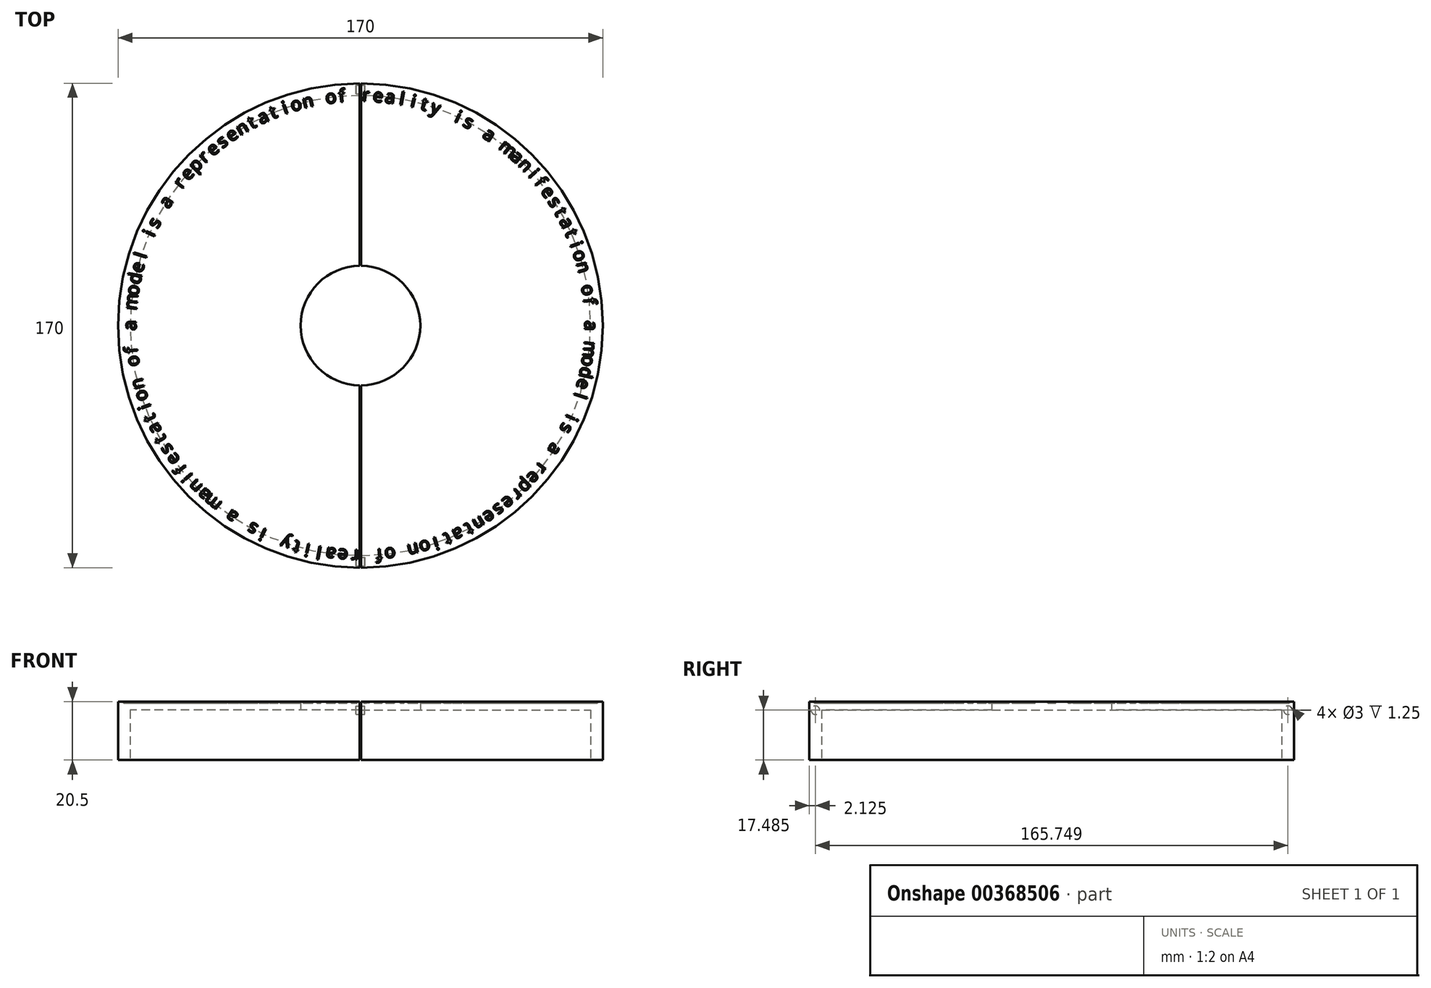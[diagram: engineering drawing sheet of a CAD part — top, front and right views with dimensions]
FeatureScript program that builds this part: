
annotation { "Feature Type Name" : "Feature", "Feature Type Description" : "" }
export const myFeature = defineFeature(function(context is Context, id is Id, definition is map)
    precondition{}
    {
        {
            var Q0;
            Q0=qCreatedBy(makeId("Front.planeOp"),FACE);
            var sketch = newSketch(context, id + "F0", { "sketchPlane" : qUnion([Q0])});
            skLineSegment(sketch, "E0", {"start": v(0, 2) * mm, "end": v(0, 7) * mm});
            skLineSegment(sketch, "E1", {"start": v(-80, 0) * mm, "end": v(-70, 0) * mm});
            skLineSegment(sketch, "E2", {"start": v(-70, 0) * mm, "end": v(-70, 2) * mm});
            skLineSegment(sketch, "E3", {"start": v(-70, 2) * mm, "end": v(0, 2) * mm});
            skLineSegment(sketch, "E4", {"start": v(0, 7) * mm, "end": v(-80, 7) * mm});
            skLineSegment(sketch, "E5", {"start": v(-80, 7) * mm, "end": v(-80, 0) * mm});
            skLineSegment(sketch, "E6.bottom", {"start": v(-21, 7) * mm, "end": v(-70, 7) * mm});
            skLineSegment(sketch, "E6.top", {"start": v(-21, 10) * mm, "end": v(-70, 10) * mm});
            skLineSegment(sketch, "E6.left", {"start": v(-21, 7) * mm, "end": v(-21, 10) * mm});
            skLineSegment(sketch, "E6.right", {"start": v(-70, 7) * mm, "end": v(-70, 10) * mm});
            skLineSegment(sketch, "E7", {"start": v(-20, 53.98) * mm, "end": v(-20, 0) * mm});
            skLineSegment(sketch, "E8", {"start": v(-20, 0) * mm, "end": v(20, 0) * mm});
            skLineSegment(sketch, "E9", {"start": v(20, 0) * mm, "end": v(20, 53.98) * mm});
            skLineSegment(sketch, "E10", {"start": v(20, 53.98) * mm, "end": v(-20, 53.98) * mm});
            skLineSegment(sketch, "E11.bottom", {"start": v(-21, 10.5) * mm, "end": v(-70.75, 10.5) * mm});
            skLineSegment(sketch, "E11.top", {"start": v(-21, 13.5) * mm, "end": v(-75, 13.5) * mm});
            skLineSegment(sketch, "E11.left", {"start": v(-21, 10.5) * mm, "end": v(-21, 13.5) * mm});
            skLineSegment(sketch, "E12.bottom", {"start": v(-21, 14) * mm, "end": v(-75.75, 14) * mm});
            skLineSegment(sketch, "E12.top", {"start": v(-21, 17) * mm, "end": v(-80, 17) * mm});
            skLineSegment(sketch, "E12.left", {"start": v(-21, 14) * mm, "end": v(-21, 17) * mm});
            skLineSegment(sketch, "E13.top", {"start": v(-80, 7) * mm, "end": v(-75.75, 7) * mm});
            skLineSegment(sketch, "E13.left", {"start": v(-80, 17) * mm, "end": v(-80, 7) * mm});
            skLineSegment(sketch, "E13.right", {"start": v(-75.75, 14) * mm, "end": v(-75.75, 7) * mm});
            skLineSegment(sketch, "E14.top", {"start": v(-75, 7) * mm, "end": v(-70.75, 7) * mm});
            skLineSegment(sketch, "E14.left", {"start": v(-75, 13.5) * mm, "end": v(-75, 7) * mm});
            skLineSegment(sketch, "E14.right", {"start": v(-70.75, 10.5) * mm, "end": v(-70.75, 7) * mm});
            skLineSegment(sketch, "E15.bottom", {"start": v(-21, 17.5) * mm, "end": v(-80.75, 17.5) * mm});
            skLineSegment(sketch, "E15.top", {"start": v(-21, 20.5) * mm, "end": v(-85, 20.5) * mm});
            skLineSegment(sketch, "E15.left", {"start": v(-21, 17.5) * mm, "end": v(-21, 20.5) * mm});
            skLineSegment(sketch, "E15.right", {"start": v(-85, 0) * mm, "end": v(-85, 20.5) * mm});
            skLineSegment(sketch, "E16.bottom", {"start": v(-85, 20.5) * mm, "end": v(-80.75, 20.5) * mm});
            skLineSegment(sketch, "E16.top", {"start": v(-85, 0) * mm, "end": v(-80.75, 0) * mm});
            skLineSegment(sketch, "E16.right", {"start": v(-80.75, 17.5) * mm, "end": v(-80.75, 0) * mm});
            skSolve(sketch);
        }
        {
            var Q0;
            Q0=makeQuery(id+"F0.imprint","IMPRINT",FACE,{"disambiguationData":[TD([[makeQuery(id+"F0.imprint","IMPRINT",EDGE,{"derivedFrom":sQuery(id+"F0.wireOp",EDGE,"E15.bottom")}),-1.0]])]});
            var Q1;
            Q1=sQuery(id+"F0.wireOp",EDGE,"E0");
            revolve(context, id + "F1", {"entities" : qUnion([Q0]), "axis" : qUnion([Q1]), "revolveType" : RevolveType.FULL});
        }
        {
            var Q0;
            Q0=makeQuery(id+"F1.opRevolve","SWEPT_FACE",FACE,{"disambiguationData":[OSD([sQuery(id+"F0.wireOp",EDGE,"E15.top"),sQuery(id+"F0.wireOp",EDGE,"E16.bottom")])]});
            var sketch = newSketch(context, id + "F2", { "sketchPlane" : qUnion([Q0])});
            skLineSegment(sketch, "E17", {"start": v(0, 0) * mm, "end": v(0, 95.11) * mm, "construction": true});
            skLineSegment(sketch, "E18.bottom", {"start": v(-1.66, 80.82) * mm, "end": v(1.34, 80.82) * mm, "construction": true});
            skLineSegment(sketch, "E18.top", {"start": v(-1.66, 76.82) * mm, "end": v(1.34, 76.82) * mm, "construction": true});
            skLineSegment(sketch, "E18.left", {"start": v(-1.66, 80.82) * mm, "end": v(-1.66, 76.82) * mm, "construction": true});
            skLineSegment(sketch, "E18.right", {"start": v(1.34, 80.82) * mm, "end": v(1.34, 76.82) * mm, "construction": true});
            skLineSegment(sketch, "E19.1.0", {"start": v(-5.82, 80.63) * mm, "end": v(-2.82, 80.78) * mm, "construction": true});
            skLineSegment(sketch, "E19.1.1", {"start": v(-2.82, 80.78) * mm, "end": v(-2.61, 76.79) * mm, "construction": true});
            skLineSegment(sketch, "E19.1.2", {"start": v(-5.6, 76.64) * mm, "end": v(-2.61, 76.79) * mm, "construction": true});
            skLineSegment(sketch, "E19.1.3", {"start": v(-5.82, 80.63) * mm, "end": v(-5.6, 76.64) * mm, "construction": true});
            skLineSegment(sketch, "E19.2.0", {"start": v(-9.96, 80.22) * mm, "end": v(-6.97, 80.53) * mm, "construction": true});
            skLineSegment(sketch, "E19.2.1", {"start": v(-6.97, 80.53) * mm, "end": v(-6.56, 76.55) * mm, "construction": true});
            skLineSegment(sketch, "E19.2.2", {"start": v(-9.55, 76.25) * mm, "end": v(-6.56, 76.55) * mm, "construction": true});
            skLineSegment(sketch, "E19.2.3", {"start": v(-9.96, 80.22) * mm, "end": v(-9.55, 76.25) * mm, "construction": true});
            skLineSegment(sketch, "E19.3.0", {"start": v(-14.08, 79.6) * mm, "end": v(-11.11, 80.07) * mm, "construction": true});
            skLineSegment(sketch, "E19.3.1", {"start": v(-11.11, 80.07) * mm, "end": v(-10.5, 76.11) * mm, "construction": true});
            skLineSegment(sketch, "E19.3.2", {"start": v(-13.46, 75.65) * mm, "end": v(-10.5, 76.11) * mm, "construction": true});
            skLineSegment(sketch, "E19.3.3", {"start": v(-14.08, 79.6) * mm, "end": v(-13.46, 75.65) * mm, "construction": true});
            skLineSegment(sketch, "E19.4.0", {"start": v(-18.15, 78.77) * mm, "end": v(-15.22, 79.39) * mm, "construction": true});
            skLineSegment(sketch, "E19.4.1", {"start": v(-15.22, 79.39) * mm, "end": v(-14.4, 75.47) * mm, "construction": true});
            skLineSegment(sketch, "E19.4.2", {"start": v(-17.34, 74.86) * mm, "end": v(-14.4, 75.47) * mm, "construction": true});
            skLineSegment(sketch, "E19.4.3", {"start": v(-18.15, 78.77) * mm, "end": v(-17.34, 74.86) * mm, "construction": true});
            skLineSegment(sketch, "E19.5.0", {"start": v(-22.19, 77.74) * mm, "end": v(-19.28, 78.5) * mm, "construction": true});
            skLineSegment(sketch, "E19.5.1", {"start": v(-19.28, 78.5) * mm, "end": v(-18.27, 74.63) * mm, "construction": true});
            skLineSegment(sketch, "E19.5.2", {"start": v(-21.17, 73.87) * mm, "end": v(-18.27, 74.63) * mm, "construction": true});
            skLineSegment(sketch, "E19.5.3", {"start": v(-22.19, 77.74) * mm, "end": v(-21.17, 73.87) * mm, "construction": true});
            skLineSegment(sketch, "E19.6.0", {"start": v(-26.16, 76.5) * mm, "end": v(-23.3, 77.4) * mm, "construction": true});
            skLineSegment(sketch, "E19.6.1", {"start": v(-23.3, 77.4) * mm, "end": v(-22.08, 73.6) * mm, "construction": true});
            skLineSegment(sketch, "E19.6.2", {"start": v(-24.94, 72.68) * mm, "end": v(-22.08, 73.6) * mm, "construction": true});
            skLineSegment(sketch, "E19.6.3", {"start": v(-26.16, 76.5) * mm, "end": v(-24.94, 72.68) * mm, "construction": true});
            skLineSegment(sketch, "E19.7.0", {"start": v(-30.06, 75.04) * mm, "end": v(-27.25, 76.1) * mm, "construction": true});
            skLineSegment(sketch, "E19.7.1", {"start": v(-27.25, 76.1) * mm, "end": v(-25.84, 72.36) * mm, "construction": true});
            skLineSegment(sketch, "E19.7.2", {"start": v(-28.65, 71.3) * mm, "end": v(-25.84, 72.36) * mm, "construction": true});
            skLineSegment(sketch, "E19.7.3", {"start": v(-30.06, 75.04) * mm, "end": v(-28.65, 71.3) * mm, "construction": true});
            skLineSegment(sketch, "E19.8.0", {"start": v(-33.88, 73.4) * mm, "end": v(-31.14, 74.6) * mm, "construction": true});
            skLineSegment(sketch, "E19.8.1", {"start": v(-31.14, 74.6) * mm, "end": v(-29.53, 70.93) * mm, "construction": true});
            skLineSegment(sketch, "E19.8.2", {"start": v(-32.28, 69.73) * mm, "end": v(-29.53, 70.93) * mm, "construction": true});
            skLineSegment(sketch, "E19.8.3", {"start": v(-33.88, 73.4) * mm, "end": v(-32.28, 69.73) * mm, "construction": true});
            skLineSegment(sketch, "E19.9.0", {"start": v(-37.62, 71.55) * mm, "end": v(-34.93, 72.9) * mm, "construction": true});
            skLineSegment(sketch, "E19.9.1", {"start": v(-34.93, 72.9) * mm, "end": v(-33.15, 69.32) * mm, "construction": true});
            skLineSegment(sketch, "E19.9.2", {"start": v(-35.83, 67.98) * mm, "end": v(-33.15, 69.32) * mm, "construction": true});
            skLineSegment(sketch, "E19.9.3", {"start": v(-37.62, 71.55) * mm, "end": v(-35.83, 67.98) * mm, "construction": true});
            skLineSegment(sketch, "E19.10.0", {"start": v(-41.25, 69.52) * mm, "end": v(-38.64, 71) * mm, "construction": true});
            skLineSegment(sketch, "E19.10.1", {"start": v(-38.64, 71) * mm, "end": v(-36.67, 67.52) * mm, "construction": true});
            skLineSegment(sketch, "E19.10.2", {"start": v(-39.28, 66.04) * mm, "end": v(-36.67, 67.52) * mm, "construction": true});
            skLineSegment(sketch, "E19.10.3", {"start": v(-41.25, 69.52) * mm, "end": v(-39.28, 66.04) * mm, "construction": true});
            skLineSegment(sketch, "E19.11.0", {"start": v(-44.78, 67.3) * mm, "end": v(-42.24, 68.92) * mm, "construction": true});
            skLineSegment(sketch, "E19.11.1", {"start": v(-42.24, 68.92) * mm, "end": v(-40.1, 65.54) * mm, "construction": true});
            skLineSegment(sketch, "E19.11.2", {"start": v(-42.63, 63.93) * mm, "end": v(-40.1, 65.54) * mm, "construction": true});
            skLineSegment(sketch, "E19.11.3", {"start": v(-44.78, 67.3) * mm, "end": v(-42.63, 63.93) * mm, "construction": true});
            skLineSegment(sketch, "E19.12.0", {"start": v(-48.18, 64.91) * mm, "end": v(-45.74, 66.65) * mm, "construction": true});
            skLineSegment(sketch, "E19.12.1", {"start": v(-45.74, 66.65) * mm, "end": v(-43.42, 63.4) * mm, "construction": true});
            skLineSegment(sketch, "E19.12.2", {"start": v(-45.86, 61.65) * mm, "end": v(-43.42, 63.4) * mm, "construction": true});
            skLineSegment(sketch, "E19.12.3", {"start": v(-48.18, 64.91) * mm, "end": v(-45.86, 61.65) * mm, "construction": true});
            skLineSegment(sketch, "E19.13.0", {"start": v(-51.46, 62.35) * mm, "end": v(-49.1, 64.2) * mm, "construction": true});
            skLineSegment(sketch, "E19.13.1", {"start": v(-49.1, 64.2) * mm, "end": v(-46.62, 61.07) * mm, "construction": true});
            skLineSegment(sketch, "E19.13.2", {"start": v(-48.98, 59.2) * mm, "end": v(-46.62, 61.07) * mm, "construction": true});
            skLineSegment(sketch, "E19.13.3", {"start": v(-51.46, 62.35) * mm, "end": v(-48.98, 59.2) * mm, "construction": true});
            skLineSegment(sketch, "E19.14.0", {"start": v(-54.6, 59.61) * mm, "end": v(-52.35, 61.6) * mm, "construction": true});
            skLineSegment(sketch, "E19.14.1", {"start": v(-52.35, 61.6) * mm, "end": v(-49.7, 58.6) * mm, "construction": true});
            skLineSegment(sketch, "E19.14.2", {"start": v(-51.96, 56.6) * mm, "end": v(-49.7, 58.6) * mm, "construction": true});
            skLineSegment(sketch, "E19.14.3", {"start": v(-54.6, 59.61) * mm, "end": v(-51.96, 56.6) * mm, "construction": true});
            skLineSegment(sketch, "E19.15.0", {"start": v(-57.6, 56.72) * mm, "end": v(-55.45, 58.82) * mm, "construction": true});
            skLineSegment(sketch, "E19.15.1", {"start": v(-55.45, 58.82) * mm, "end": v(-52.66, 55.95) * mm, "construction": true});
            skLineSegment(sketch, "E19.15.2", {"start": v(-54.8, 53.86) * mm, "end": v(-52.66, 55.95) * mm, "construction": true});
            skLineSegment(sketch, "E19.15.3", {"start": v(-57.6, 56.72) * mm, "end": v(-54.8, 53.86) * mm, "construction": true});
            skLineSegment(sketch, "E19.16.0", {"start": v(-60.44, 53.68) * mm, "end": v(-58.4, 55.89) * mm, "construction": true});
            skLineSegment(sketch, "E19.16.1", {"start": v(-58.4, 55.89) * mm, "end": v(-55.47, 53.17) * mm, "construction": true});
            skLineSegment(sketch, "E19.16.2", {"start": v(-57.5, 50.97) * mm, "end": v(-55.47, 53.17) * mm, "construction": true});
            skLineSegment(sketch, "E19.16.3", {"start": v(-60.44, 53.68) * mm, "end": v(-57.5, 50.97) * mm, "construction": true});
            skLineSegment(sketch, "E19.17.0", {"start": v(-63.12, 50.5) * mm, "end": v(-61.2, 52.8) * mm, "construction": true});
            skLineSegment(sketch, "E19.17.1", {"start": v(-61.2, 52.8) * mm, "end": v(-58.13, 50.24) * mm, "construction": true});
            skLineSegment(sketch, "E19.17.2", {"start": v(-60.05, 47.94) * mm, "end": v(-58.13, 50.24) * mm, "construction": true});
            skLineSegment(sketch, "E19.17.3", {"start": v(-63.12, 50.5) * mm, "end": v(-60.05, 47.94) * mm, "construction": true});
            skLineSegment(sketch, "E19.18.0", {"start": v(-65.64, 47.19) * mm, "end": v(-63.84, 49.58) * mm, "construction": true});
            skLineSegment(sketch, "E19.18.1", {"start": v(-63.84, 49.58) * mm, "end": v(-60.64, 47.18) * mm, "construction": true});
            skLineSegment(sketch, "E19.18.2", {"start": v(-62.44, 44.78) * mm, "end": v(-60.64, 47.18) * mm, "construction": true});
            skLineSegment(sketch, "E19.18.3", {"start": v(-65.64, 47.19) * mm, "end": v(-62.44, 44.78) * mm, "construction": true});
            skLineSegment(sketch, "E19.19.0", {"start": v(-67.98, 43.74) * mm, "end": v(-66.3, 46.23) * mm, "construction": true});
            skLineSegment(sketch, "E19.19.1", {"start": v(-66.3, 46.23) * mm, "end": v(-62.99, 44) * mm, "construction": true});
            skLineSegment(sketch, "E19.19.2", {"start": v(-64.66, 41.51) * mm, "end": v(-62.99, 44) * mm, "construction": true});
            skLineSegment(sketch, "E19.19.3", {"start": v(-67.98, 43.74) * mm, "end": v(-64.66, 41.51) * mm, "construction": true});
            skLineSegment(sketch, "E19.20.0", {"start": v(-70.14, 40.19) * mm, "end": v(-68.6, 42.76) * mm, "construction": true});
            skLineSegment(sketch, "E19.20.1", {"start": v(-68.6, 42.76) * mm, "end": v(-65.17, 40.7) * mm, "construction": true});
            skLineSegment(sketch, "E19.20.2", {"start": v(-66.71, 38.13) * mm, "end": v(-65.17, 40.7) * mm, "construction": true});
            skLineSegment(sketch, "E19.20.3", {"start": v(-70.14, 40.19) * mm, "end": v(-66.71, 38.13) * mm, "construction": true});
            skLineSegment(sketch, "E19.21.0", {"start": v(-72.12, 36.52) * mm, "end": v(-70.7, 39.17) * mm, "construction": true});
            skLineSegment(sketch, "E19.21.1", {"start": v(-70.7, 39.17) * mm, "end": v(-67.18, 37.3) * mm, "construction": true});
            skLineSegment(sketch, "E19.21.2", {"start": v(-68.59, 34.64) * mm, "end": v(-67.18, 37.3) * mm, "construction": true});
            skLineSegment(sketch, "E19.21.3", {"start": v(-72.12, 36.52) * mm, "end": v(-68.59, 34.64) * mm, "construction": true});
            skLineSegment(sketch, "E19.22.0", {"start": v(-73.9, 32.76) * mm, "end": v(-72.63, 35.48) * mm, "construction": true});
            skLineSegment(sketch, "E19.22.1", {"start": v(-72.63, 35.48) * mm, "end": v(-69, 33.78) * mm, "construction": true});
            skLineSegment(sketch, "E19.22.2", {"start": v(-70.28, 31.07) * mm, "end": v(-69, 33.78) * mm, "construction": true});
            skLineSegment(sketch, "E19.22.3", {"start": v(-73.9, 32.76) * mm, "end": v(-70.28, 31.07) * mm, "construction": true});
            skLineSegment(sketch, "E19.23.0", {"start": v(-75.5, 28.91) * mm, "end": v(-74.36, 31.7) * mm, "construction": true});
            skLineSegment(sketch, "E19.23.1", {"start": v(-74.36, 31.7) * mm, "end": v(-70.66, 30.19) * mm, "construction": true});
            skLineSegment(sketch, "E19.23.2", {"start": v(-71.79, 27.4) * mm, "end": v(-70.66, 30.19) * mm, "construction": true});
            skLineSegment(sketch, "E19.23.3", {"start": v(-75.5, 28.91) * mm, "end": v(-71.79, 27.4) * mm, "construction": true});
            skLineSegment(sketch, "E19.24.0", {"start": v(-76.88, 24.99) * mm, "end": v(-75.9, 27.82) * mm, "construction": true});
            skLineSegment(sketch, "E19.24.1", {"start": v(-75.9, 27.82) * mm, "end": v(-72.12, 26.5) * mm, "construction": true});
            skLineSegment(sketch, "E19.24.2", {"start": v(-73.1, 23.67) * mm, "end": v(-72.12, 26.5) * mm, "construction": true});
            skLineSegment(sketch, "E19.24.3", {"start": v(-76.88, 24.99) * mm, "end": v(-73.1, 23.67) * mm, "construction": true});
            skLineSegment(sketch, "E19.25.0", {"start": v(-78.07, 21) * mm, "end": v(-77.23, 23.88) * mm, "construction": true});
            skLineSegment(sketch, "E19.25.1", {"start": v(-77.23, 23.88) * mm, "end": v(-73.39, 22.76) * mm, "construction": true});
            skLineSegment(sketch, "E19.25.2", {"start": v(-74.22, 19.88) * mm, "end": v(-73.39, 22.76) * mm, "construction": true});
            skLineSegment(sketch, "E19.25.3", {"start": v(-78.07, 21) * mm, "end": v(-74.22, 19.88) * mm, "construction": true});
            skLineSegment(sketch, "E19.26.0", {"start": v(-79.04, 16.95) * mm, "end": v(-78.35, 19.87) * mm, "construction": true});
            skLineSegment(sketch, "E19.26.1", {"start": v(-78.35, 19.87) * mm, "end": v(-74.46, 18.95) * mm, "construction": true});
            skLineSegment(sketch, "E19.26.2", {"start": v(-75.15, 16.03) * mm, "end": v(-74.46, 18.95) * mm, "construction": true});
            skLineSegment(sketch, "E19.26.3", {"start": v(-79.04, 16.95) * mm, "end": v(-75.15, 16.03) * mm, "construction": true});
            skLineSegment(sketch, "E19.27.0", {"start": v(-79.81, 12.86) * mm, "end": v(-79.27, 15.81) * mm, "construction": true});
            skLineSegment(sketch, "E19.27.1", {"start": v(-79.27, 15.81) * mm, "end": v(-75.34, 15.1) * mm, "construction": true});
            skLineSegment(sketch, "E19.27.2", {"start": v(-75.88, 12.14) * mm, "end": v(-75.34, 15.1) * mm, "construction": true});
            skLineSegment(sketch, "E19.27.3", {"start": v(-79.81, 12.86) * mm, "end": v(-75.88, 12.14) * mm, "construction": true});
            skLineSegment(sketch, "E19.28.0", {"start": v(-80.37, 8.73) * mm, "end": v(-79.98, 11.7) * mm, "construction": true});
            skLineSegment(sketch, "E19.28.1", {"start": v(-79.98, 11.7) * mm, "end": v(-76.01, 11.2) * mm, "construction": true});
            skLineSegment(sketch, "E19.28.2", {"start": v(-76.4, 8.22) * mm, "end": v(-76.01, 11.2) * mm, "construction": true});
            skLineSegment(sketch, "E19.28.3", {"start": v(-80.37, 8.73) * mm, "end": v(-76.4, 8.22) * mm, "construction": true});
            skLineSegment(sketch, "E19.29.0", {"start": v(-80.7, 4.59) * mm, "end": v(-80.48, 7.58) * mm, "construction": true});
            skLineSegment(sketch, "E19.29.1", {"start": v(-80.48, 7.58) * mm, "end": v(-76.49, 7.27) * mm, "construction": true});
            skLineSegment(sketch, "E19.29.2", {"start": v(-76.72, 4.28) * mm, "end": v(-76.49, 7.27) * mm, "construction": true});
            skLineSegment(sketch, "E19.29.3", {"start": v(-80.7, 4.59) * mm, "end": v(-76.72, 4.28) * mm, "construction": true});
            skLineSegment(sketch, "E19.30.0", {"start": v(-80.84, 0.42) * mm, "end": v(-80.76, 3.42) * mm, "construction": true});
            skLineSegment(sketch, "E19.30.1", {"start": v(-80.76, 3.42) * mm, "end": v(-76.76, 3.32) * mm, "construction": true});
            skLineSegment(sketch, "E19.30.2", {"start": v(-76.84, 0.32) * mm, "end": v(-76.76, 3.32) * mm, "construction": true});
            skLineSegment(sketch, "E19.30.3", {"start": v(-80.84, 0.42) * mm, "end": v(-76.84, 0.32) * mm, "construction": true});
            skLineSegment(sketch, "E19.31.0", {"start": v(-80.75, -3.74) * mm, "end": v(-80.83, -0.74) * mm, "construction": true});
            skLineSegment(sketch, "E19.31.1", {"start": v(-80.83, -0.74) * mm, "end": v(-76.83, -0.64) * mm, "construction": true});
            skLineSegment(sketch, "E19.31.2", {"start": v(-76.75, -3.63) * mm, "end": v(-76.83, -0.64) * mm, "construction": true});
            skLineSegment(sketch, "E19.31.3", {"start": v(-80.75, -3.74) * mm, "end": v(-76.75, -3.63) * mm, "construction": true});
            skLineSegment(sketch, "E19.32.0", {"start": v(-80.45, -7.89) * mm, "end": v(-80.69, -4.9) * mm, "construction": true});
            skLineSegment(sketch, "E19.32.1", {"start": v(-80.69, -4.9) * mm, "end": v(-76.7, -4.6) * mm, "construction": true});
            skLineSegment(sketch, "E19.32.2", {"start": v(-76.47, -7.58) * mm, "end": v(-76.7, -4.6) * mm, "construction": true});
            skLineSegment(sketch, "E19.32.3", {"start": v(-80.45, -7.89) * mm, "end": v(-76.47, -7.58) * mm, "construction": true});
            skLineSegment(sketch, "E19.33.0", {"start": v(-79.94, -12.02) * mm, "end": v(-80.33, -9.05) * mm, "construction": true});
            skLineSegment(sketch, "E19.33.1", {"start": v(-80.33, -9.05) * mm, "end": v(-76.36, -8.53) * mm, "construction": true});
            skLineSegment(sketch, "E19.33.2", {"start": v(-75.97, -11.5) * mm, "end": v(-76.36, -8.53) * mm, "construction": true});
            skLineSegment(sketch, "E19.33.3", {"start": v(-79.94, -12.02) * mm, "end": v(-75.97, -11.5) * mm, "construction": true});
            skLineSegment(sketch, "E19.34.0", {"start": v(-79.22, -16.12) * mm, "end": v(-79.75, -13.17) * mm, "construction": true});
            skLineSegment(sketch, "E19.34.1", {"start": v(-79.75, -13.17) * mm, "end": v(-75.82, -12.45) * mm, "construction": true});
            skLineSegment(sketch, "E19.34.2", {"start": v(-75.28, -15.4) * mm, "end": v(-75.82, -12.45) * mm, "construction": true});
            skLineSegment(sketch, "E19.34.3", {"start": v(-79.22, -16.12) * mm, "end": v(-75.28, -15.4) * mm, "construction": true});
            skLineSegment(sketch, "E19.35.0", {"start": v(-78.28, -20.18) * mm, "end": v(-78.97, -17.26) * mm, "construction": true});
            skLineSegment(sketch, "E19.35.1", {"start": v(-78.97, -17.26) * mm, "end": v(-75.08, -16.34) * mm, "construction": true});
            skLineSegment(sketch, "E19.35.2", {"start": v(-74.39, -19.26) * mm, "end": v(-75.08, -16.34) * mm, "construction": true});
            skLineSegment(sketch, "E19.35.3", {"start": v(-78.28, -20.18) * mm, "end": v(-74.39, -19.26) * mm, "construction": true});
            skLineSegment(sketch, "E19.36.0", {"start": v(-77.14, -24.18) * mm, "end": v(-77.98, -21.3) * mm, "construction": true});
            skLineSegment(sketch, "E19.36.1", {"start": v(-77.98, -21.3) * mm, "end": v(-74.14, -20.18) * mm, "construction": true});
            skLineSegment(sketch, "E19.36.2", {"start": v(-73.3, -23.06) * mm, "end": v(-74.14, -20.18) * mm, "construction": true});
            skLineSegment(sketch, "E19.36.3", {"start": v(-77.14, -24.18) * mm, "end": v(-73.3, -23.06) * mm, "construction": true});
            skLineSegment(sketch, "E19.37.0", {"start": v(-75.8, -28.12) * mm, "end": v(-76.78, -25.29) * mm, "construction": true});
            skLineSegment(sketch, "E19.37.1", {"start": v(-76.78, -25.29) * mm, "end": v(-73, -23.97) * mm, "construction": true});
            skLineSegment(sketch, "E19.37.2", {"start": v(-72.01, -26.8) * mm, "end": v(-73, -23.97) * mm, "construction": true});
            skLineSegment(sketch, "E19.37.3", {"start": v(-75.8, -28.12) * mm, "end": v(-72.01, -26.8) * mm, "construction": true});
            skLineSegment(sketch, "E19.38.0", {"start": v(-74.24, -31.98) * mm, "end": v(-75.37, -29.2) * mm, "construction": true});
            skLineSegment(sketch, "E19.38.1", {"start": v(-75.37, -29.2) * mm, "end": v(-71.67, -27.7) * mm, "construction": true});
            skLineSegment(sketch, "E19.38.2", {"start": v(-70.54, -30.48) * mm, "end": v(-71.67, -27.7) * mm, "construction": true});
            skLineSegment(sketch, "E19.38.3", {"start": v(-74.24, -31.98) * mm, "end": v(-70.54, -30.48) * mm, "construction": true});
            skLineSegment(sketch, "E19.39.0", {"start": v(-72.5, -35.76) * mm, "end": v(-73.77, -33.05) * mm, "construction": true});
            skLineSegment(sketch, "E19.39.1", {"start": v(-73.77, -33.05) * mm, "end": v(-70.15, -31.35) * mm, "construction": true});
            skLineSegment(sketch, "E19.39.2", {"start": v(-68.88, -34.07) * mm, "end": v(-70.15, -31.35) * mm, "construction": true});
            skLineSegment(sketch, "E19.39.3", {"start": v(-72.5, -35.76) * mm, "end": v(-68.88, -34.07) * mm, "construction": true});
            skLineSegment(sketch, "E19.40.0", {"start": v(-70.56, -39.45) * mm, "end": v(-71.97, -36.8) * mm, "construction": true});
            skLineSegment(sketch, "E19.40.1", {"start": v(-71.97, -36.8) * mm, "end": v(-68.44, -34.92) * mm, "construction": true});
            skLineSegment(sketch, "E19.40.2", {"start": v(-67.03, -37.57) * mm, "end": v(-68.44, -34.92) * mm, "construction": true});
            skLineSegment(sketch, "E19.40.3", {"start": v(-70.56, -39.45) * mm, "end": v(-67.03, -37.57) * mm, "construction": true});
            skLineSegment(sketch, "E19.41.0", {"start": v(-68.44, -43.03) * mm, "end": v(-69.98, -40.46) * mm, "construction": true});
            skLineSegment(sketch, "E19.41.1", {"start": v(-69.98, -40.46) * mm, "end": v(-66.55, -38.4) * mm, "construction": true});
            skLineSegment(sketch, "E19.41.2", {"start": v(-65, -40.97) * mm, "end": v(-66.55, -38.4) * mm, "construction": true});
            skLineSegment(sketch, "E19.41.3", {"start": v(-68.44, -43.03) * mm, "end": v(-65, -40.97) * mm, "construction": true});
            skLineSegment(sketch, "E19.42.0", {"start": v(-66.13, -46.5) * mm, "end": v(-67.8, -44) * mm, "construction": true});
            skLineSegment(sketch, "E19.42.1", {"start": v(-67.8, -44) * mm, "end": v(-64.49, -41.77) * mm, "construction": true});
            skLineSegment(sketch, "E19.42.2", {"start": v(-62.81, -44.26) * mm, "end": v(-64.49, -41.77) * mm, "construction": true});
            skLineSegment(sketch, "E19.42.3", {"start": v(-66.13, -46.5) * mm, "end": v(-62.81, -44.26) * mm, "construction": true});
            skLineSegment(sketch, "E19.43.0", {"start": v(-63.65, -49.84) * mm, "end": v(-65.45, -47.44) * mm, "construction": true});
            skLineSegment(sketch, "E19.43.1", {"start": v(-65.45, -47.44) * mm, "end": v(-62.25, -45.04) * mm, "construction": true});
            skLineSegment(sketch, "E19.43.2", {"start": v(-60.45, -47.44) * mm, "end": v(-62.25, -45.04) * mm, "construction": true});
            skLineSegment(sketch, "E19.43.3", {"start": v(-63.65, -49.84) * mm, "end": v(-60.45, -47.44) * mm, "construction": true});
            skLineSegment(sketch, "E19.44.0", {"start": v(-61, -53.05) * mm, "end": v(-62.92, -50.74) * mm, "construction": true});
            skLineSegment(sketch, "E19.44.1", {"start": v(-62.92, -50.74) * mm, "end": v(-59.85, -48.18) * mm, "construction": true});
            skLineSegment(sketch, "E19.44.2", {"start": v(-57.93, -50.48) * mm, "end": v(-59.85, -48.18) * mm, "construction": true});
            skLineSegment(sketch, "E19.44.3", {"start": v(-61, -53.05) * mm, "end": v(-57.93, -50.48) * mm, "construction": true});
            skLineSegment(sketch, "E19.45.0", {"start": v(-58.19, -56.12) * mm, "end": v(-60.23, -53.92) * mm, "construction": true});
            skLineSegment(sketch, "E19.45.1", {"start": v(-60.23, -53.92) * mm, "end": v(-57.3, -51.2) * mm, "construction": true});
            skLineSegment(sketch, "E19.45.2", {"start": v(-55.25, -53.4) * mm, "end": v(-57.3, -51.2) * mm, "construction": true});
            skLineSegment(sketch, "E19.45.3", {"start": v(-58.19, -56.12) * mm, "end": v(-55.25, -53.4) * mm, "construction": true});
            skLineSegment(sketch, "E19.46.0", {"start": v(-55.22, -59.04) * mm, "end": v(-57.37, -56.94) * mm, "construction": true});
            skLineSegment(sketch, "E19.46.1", {"start": v(-57.37, -56.94) * mm, "end": v(-54.58, -54.08) * mm, "construction": true});
            skLineSegment(sketch, "E19.46.2", {"start": v(-52.43, -56.17) * mm, "end": v(-54.58, -54.08) * mm, "construction": true});
            skLineSegment(sketch, "E19.46.3", {"start": v(-55.22, -59.04) * mm, "end": v(-52.43, -56.17) * mm, "construction": true});
            skLineSegment(sketch, "E19.47.0", {"start": v(-52.11, -61.8) * mm, "end": v(-54.36, -59.82) * mm, "construction": true});
            skLineSegment(sketch, "E19.47.1", {"start": v(-54.36, -59.82) * mm, "end": v(-51.72, -56.82) * mm, "construction": true});
            skLineSegment(sketch, "E19.47.2", {"start": v(-49.47, -58.8) * mm, "end": v(-51.72, -56.82) * mm, "construction": true});
            skLineSegment(sketch, "E19.47.3", {"start": v(-52.11, -61.8) * mm, "end": v(-49.47, -58.8) * mm, "construction": true});
            skLineSegment(sketch, "E19.48.0", {"start": v(-48.86, -64.4) * mm, "end": v(-51.21, -62.54) * mm, "construction": true});
            skLineSegment(sketch, "E19.48.1", {"start": v(-51.21, -62.54) * mm, "end": v(-48.73, -59.4) * mm, "construction": true});
            skLineSegment(sketch, "E19.48.2", {"start": v(-46.38, -61.27) * mm, "end": v(-48.73, -59.4) * mm, "construction": true});
            skLineSegment(sketch, "E19.48.3", {"start": v(-48.86, -64.4) * mm, "end": v(-46.38, -61.27) * mm, "construction": true});
            skLineSegment(sketch, "E19.49.0", {"start": v(-45.48, -66.83) * mm, "end": v(-47.92, -65.1) * mm, "construction": true});
            skLineSegment(sketch, "E19.49.1", {"start": v(-47.92, -65.1) * mm, "end": v(-45.6, -61.83) * mm, "construction": true});
            skLineSegment(sketch, "E19.49.2", {"start": v(-43.16, -63.57) * mm, "end": v(-45.6, -61.83) * mm, "construction": true});
            skLineSegment(sketch, "E19.49.3", {"start": v(-45.48, -66.83) * mm, "end": v(-43.16, -63.57) * mm, "construction": true});
            skLineSegment(sketch, "E19.50.0", {"start": v(-41.98, -69.09) * mm, "end": v(-44.51, -67.48) * mm, "construction": true});
            skLineSegment(sketch, "E19.50.1", {"start": v(-44.51, -67.48) * mm, "end": v(-42.36, -64.1) * mm, "construction": true});
            skLineSegment(sketch, "E19.50.2", {"start": v(-39.83, -65.71) * mm, "end": v(-42.36, -64.1) * mm, "construction": true});
            skLineSegment(sketch, "E19.50.3", {"start": v(-41.98, -69.09) * mm, "end": v(-39.83, -65.71) * mm, "construction": true});
            skLineSegment(sketch, "E19.51.0", {"start": v(-38.37, -71.16) * mm, "end": v(-40.98, -69.68) * mm, "construction": true});
            skLineSegment(sketch, "E19.51.1", {"start": v(-40.98, -69.68) * mm, "end": v(-39, -66.2) * mm, "construction": true});
            skLineSegment(sketch, "E19.51.2", {"start": v(-36.4, -67.67) * mm, "end": v(-39, -66.2) * mm, "construction": true});
            skLineSegment(sketch, "E19.51.3", {"start": v(-38.37, -71.16) * mm, "end": v(-36.4, -67.67) * mm, "construction": true});
            skLineSegment(sketch, "E19.52.0", {"start": v(-34.65, -73.04) * mm, "end": v(-37.34, -71.7) * mm, "construction": true});
            skLineSegment(sketch, "E19.52.1", {"start": v(-37.34, -71.7) * mm, "end": v(-35.55, -68.12) * mm, "construction": true});
            skLineSegment(sketch, "E19.52.2", {"start": v(-32.86, -69.46) * mm, "end": v(-35.55, -68.12) * mm, "construction": true});
            skLineSegment(sketch, "E19.52.3", {"start": v(-34.65, -73.04) * mm, "end": v(-32.86, -69.46) * mm, "construction": true});
            skLineSegment(sketch, "E19.53.0", {"start": v(-30.85, -74.72) * mm, "end": v(-33.6, -73.52) * mm, "construction": true});
            skLineSegment(sketch, "E19.53.1", {"start": v(-33.6, -73.52) * mm, "end": v(-32, -69.86) * mm, "construction": true});
            skLineSegment(sketch, "E19.53.2", {"start": v(-29.25, -71.06) * mm, "end": v(-32, -69.86) * mm, "construction": true});
            skLineSegment(sketch, "E19.53.3", {"start": v(-30.85, -74.72) * mm, "end": v(-29.25, -71.06) * mm, "construction": true});
            skLineSegment(sketch, "E19.54.0", {"start": v(-26.96, -76.21) * mm, "end": v(-29.77, -75.15) * mm, "construction": true});
            skLineSegment(sketch, "E19.54.1", {"start": v(-29.77, -75.15) * mm, "end": v(-28.36, -71.41) * mm, "construction": true});
            skLineSegment(sketch, "E19.54.2", {"start": v(-25.55, -72.47) * mm, "end": v(-28.36, -71.41) * mm, "construction": true});
            skLineSegment(sketch, "E19.54.3", {"start": v(-26.96, -76.21) * mm, "end": v(-25.55, -72.47) * mm, "construction": true});
            skLineSegment(sketch, "E19.55.0", {"start": v(-23, -77.5) * mm, "end": v(-25.86, -76.59) * mm, "construction": true});
            skLineSegment(sketch, "E19.55.1", {"start": v(-25.86, -76.59) * mm, "end": v(-24.64, -72.78) * mm, "construction": true});
            skLineSegment(sketch, "E19.55.2", {"start": v(-21.78, -73.69) * mm, "end": v(-24.64, -72.78) * mm, "construction": true});
            skLineSegment(sketch, "E19.55.3", {"start": v(-23, -77.5) * mm, "end": v(-21.78, -73.69) * mm, "construction": true});
            skLineSegment(sketch, "E19.56.0", {"start": v(-18.98, -78.58) * mm, "end": v(-21.88, -77.82) * mm, "construction": true});
            skLineSegment(sketch, "E19.56.1", {"start": v(-21.88, -77.82) * mm, "end": v(-20.86, -73.95) * mm, "construction": true});
            skLineSegment(sketch, "E19.56.2", {"start": v(-17.96, -74.71) * mm, "end": v(-20.86, -73.95) * mm, "construction": true});
            skLineSegment(sketch, "E19.56.3", {"start": v(-18.98, -78.58) * mm, "end": v(-17.96, -74.71) * mm, "construction": true});
            skLineSegment(sketch, "E19.57.0", {"start": v(-14.91, -79.45) * mm, "end": v(-17.85, -78.84) * mm, "construction": true});
            skLineSegment(sketch, "E19.57.1", {"start": v(-17.85, -78.84) * mm, "end": v(-17.03, -74.92) * mm, "construction": true});
            skLineSegment(sketch, "E19.57.2", {"start": v(-14.1, -75.54) * mm, "end": v(-17.03, -74.92) * mm, "construction": true});
            skLineSegment(sketch, "E19.57.3", {"start": v(-14.91, -79.45) * mm, "end": v(-14.1, -75.54) * mm, "construction": true});
            skLineSegment(sketch, "E19.58.0", {"start": v(-10.8, -80.11) * mm, "end": v(-13.76, -79.65) * mm, "construction": true});
            skLineSegment(sketch, "E19.58.1", {"start": v(-13.76, -79.65) * mm, "end": v(-13.15, -75.7) * mm, "construction": true});
            skLineSegment(sketch, "E19.58.2", {"start": v(-10.18, -76.16) * mm, "end": v(-13.15, -75.7) * mm, "construction": true});
            skLineSegment(sketch, "E19.58.3", {"start": v(-10.8, -80.11) * mm, "end": v(-10.18, -76.16) * mm, "construction": true});
            skLineSegment(sketch, "E19.59.0", {"start": v(-6.66, -80.56) * mm, "end": v(-9.65, -80.26) * mm, "construction": true});
            skLineSegment(sketch, "E19.59.1", {"start": v(-9.65, -80.26) * mm, "end": v(-9.23, -76.28) * mm, "construction": true});
            skLineSegment(sketch, "E19.59.2", {"start": v(-6.25, -76.59) * mm, "end": v(-9.23, -76.28) * mm, "construction": true});
            skLineSegment(sketch, "E19.59.3", {"start": v(-6.66, -80.56) * mm, "end": v(-6.25, -76.59) * mm, "construction": true});
            skLineSegment(sketch, "E19.60.0", {"start": v(-2.5, -80.8) * mm, "end": v(-5.5, -80.65) * mm, "construction": true});
            skLineSegment(sketch, "E19.60.1", {"start": v(-5.5, -80.65) * mm, "end": v(-5.3, -76.65) * mm, "construction": true});
            skLineSegment(sketch, "E19.60.2", {"start": v(-2.3, -76.8) * mm, "end": v(-5.3, -76.65) * mm, "construction": true});
            skLineSegment(sketch, "E19.60.3", {"start": v(-2.5, -80.8) * mm, "end": v(-2.3, -76.8) * mm, "construction": true});
            skLineSegment(sketch, "E19.61.0", {"start": v(1.66, -80.82) * mm, "end": v(-1.34, -80.82) * mm, "construction": true});
            skLineSegment(sketch, "E19.61.1", {"start": v(-1.34, -80.82) * mm, "end": v(-1.34, -76.82) * mm, "construction": true});
            skLineSegment(sketch, "E19.61.2", {"start": v(1.66, -76.82) * mm, "end": v(-1.34, -76.82) * mm, "construction": true});
            skLineSegment(sketch, "E19.61.3", {"start": v(1.66, -80.82) * mm, "end": v(1.66, -76.82) * mm, "construction": true});
            skLineSegment(sketch, "E19.62.0", {"start": v(5.82, -80.63) * mm, "end": v(2.82, -80.78) * mm, "construction": true});
            skLineSegment(sketch, "E19.62.1", {"start": v(2.82, -80.78) * mm, "end": v(2.61, -76.79) * mm, "construction": true});
            skLineSegment(sketch, "E19.62.2", {"start": v(5.6, -76.64) * mm, "end": v(2.61, -76.79) * mm, "construction": true});
            skLineSegment(sketch, "E19.62.3", {"start": v(5.82, -80.63) * mm, "end": v(5.6, -76.64) * mm, "construction": true});
            skLineSegment(sketch, "E19.63.0", {"start": v(9.96, -80.22) * mm, "end": v(6.97, -80.53) * mm, "construction": true});
            skLineSegment(sketch, "E19.63.1", {"start": v(6.97, -80.53) * mm, "end": v(6.56, -76.55) * mm, "construction": true});
            skLineSegment(sketch, "E19.63.2", {"start": v(9.55, -76.25) * mm, "end": v(6.56, -76.55) * mm, "construction": true});
            skLineSegment(sketch, "E19.63.3", {"start": v(9.96, -80.22) * mm, "end": v(9.55, -76.25) * mm, "construction": true});
            skLineSegment(sketch, "E19.64.0", {"start": v(14.08, -79.6) * mm, "end": v(11.11, -80.07) * mm, "construction": true});
            skLineSegment(sketch, "E19.64.1", {"start": v(11.11, -80.07) * mm, "end": v(10.5, -76.11) * mm, "construction": true});
            skLineSegment(sketch, "E19.64.2", {"start": v(13.46, -75.65) * mm, "end": v(10.5, -76.11) * mm, "construction": true});
            skLineSegment(sketch, "E19.64.3", {"start": v(14.08, -79.6) * mm, "end": v(13.46, -75.65) * mm, "construction": true});
            skLineSegment(sketch, "E19.65.0", {"start": v(18.15, -78.77) * mm, "end": v(15.22, -79.39) * mm, "construction": true});
            skLineSegment(sketch, "E19.65.1", {"start": v(15.22, -79.39) * mm, "end": v(14.4, -75.47) * mm, "construction": true});
            skLineSegment(sketch, "E19.65.2", {"start": v(17.34, -74.86) * mm, "end": v(14.4, -75.47) * mm, "construction": true});
            skLineSegment(sketch, "E19.65.3", {"start": v(18.15, -78.77) * mm, "end": v(17.34, -74.86) * mm, "construction": true});
            skLineSegment(sketch, "E19.66.0", {"start": v(22.19, -77.74) * mm, "end": v(19.28, -78.5) * mm, "construction": true});
            skLineSegment(sketch, "E19.66.1", {"start": v(19.28, -78.5) * mm, "end": v(18.27, -74.63) * mm, "construction": true});
            skLineSegment(sketch, "E19.66.2", {"start": v(21.17, -73.87) * mm, "end": v(18.27, -74.63) * mm, "construction": true});
            skLineSegment(sketch, "E19.66.3", {"start": v(22.19, -77.74) * mm, "end": v(21.17, -73.87) * mm, "construction": true});
            skLineSegment(sketch, "E19.67.0", {"start": v(26.16, -76.5) * mm, "end": v(23.3, -77.4) * mm, "construction": true});
            skLineSegment(sketch, "E19.67.1", {"start": v(23.3, -77.4) * mm, "end": v(22.08, -73.6) * mm, "construction": true});
            skLineSegment(sketch, "E19.67.2", {"start": v(24.94, -72.68) * mm, "end": v(22.08, -73.6) * mm, "construction": true});
            skLineSegment(sketch, "E19.67.3", {"start": v(26.16, -76.5) * mm, "end": v(24.94, -72.68) * mm, "construction": true});
            skLineSegment(sketch, "E19.68.0", {"start": v(30.06, -75.04) * mm, "end": v(27.25, -76.1) * mm, "construction": true});
            skLineSegment(sketch, "E19.68.1", {"start": v(27.25, -76.1) * mm, "end": v(25.84, -72.36) * mm, "construction": true});
            skLineSegment(sketch, "E19.68.2", {"start": v(28.65, -71.3) * mm, "end": v(25.84, -72.36) * mm, "construction": true});
            skLineSegment(sketch, "E19.68.3", {"start": v(30.06, -75.04) * mm, "end": v(28.65, -71.3) * mm, "construction": true});
            skLineSegment(sketch, "E19.69.0", {"start": v(33.88, -73.4) * mm, "end": v(31.14, -74.6) * mm, "construction": true});
            skLineSegment(sketch, "E19.69.1", {"start": v(31.14, -74.6) * mm, "end": v(29.53, -70.93) * mm, "construction": true});
            skLineSegment(sketch, "E19.69.2", {"start": v(32.28, -69.73) * mm, "end": v(29.53, -70.93) * mm, "construction": true});
            skLineSegment(sketch, "E19.69.3", {"start": v(33.88, -73.4) * mm, "end": v(32.28, -69.73) * mm, "construction": true});
            skLineSegment(sketch, "E19.70.0", {"start": v(37.62, -71.55) * mm, "end": v(34.93, -72.9) * mm, "construction": true});
            skLineSegment(sketch, "E19.70.1", {"start": v(34.93, -72.9) * mm, "end": v(33.15, -69.32) * mm, "construction": true});
            skLineSegment(sketch, "E19.70.2", {"start": v(35.83, -67.98) * mm, "end": v(33.15, -69.32) * mm, "construction": true});
            skLineSegment(sketch, "E19.70.3", {"start": v(37.62, -71.55) * mm, "end": v(35.83, -67.98) * mm, "construction": true});
            skLineSegment(sketch, "E19.71.0", {"start": v(41.25, -69.52) * mm, "end": v(38.64, -71) * mm, "construction": true});
            skLineSegment(sketch, "E19.71.1", {"start": v(38.64, -71) * mm, "end": v(36.67, -67.52) * mm, "construction": true});
            skLineSegment(sketch, "E19.71.2", {"start": v(39.28, -66.04) * mm, "end": v(36.67, -67.52) * mm, "construction": true});
            skLineSegment(sketch, "E19.71.3", {"start": v(41.25, -69.52) * mm, "end": v(39.28, -66.04) * mm, "construction": true});
            skLineSegment(sketch, "E19.72.0", {"start": v(44.78, -67.3) * mm, "end": v(42.24, -68.92) * mm, "construction": true});
            skLineSegment(sketch, "E19.72.1", {"start": v(42.24, -68.92) * mm, "end": v(40.1, -65.54) * mm, "construction": true});
            skLineSegment(sketch, "E19.72.2", {"start": v(42.63, -63.93) * mm, "end": v(40.1, -65.54) * mm, "construction": true});
            skLineSegment(sketch, "E19.72.3", {"start": v(44.78, -67.3) * mm, "end": v(42.63, -63.93) * mm, "construction": true});
            skLineSegment(sketch, "E19.73.0", {"start": v(48.18, -64.91) * mm, "end": v(45.74, -66.65) * mm, "construction": true});
            skLineSegment(sketch, "E19.73.1", {"start": v(45.74, -66.65) * mm, "end": v(43.42, -63.4) * mm, "construction": true});
            skLineSegment(sketch, "E19.73.2", {"start": v(45.86, -61.65) * mm, "end": v(43.42, -63.4) * mm, "construction": true});
            skLineSegment(sketch, "E19.73.3", {"start": v(48.18, -64.91) * mm, "end": v(45.86, -61.65) * mm, "construction": true});
            skLineSegment(sketch, "E19.74.0", {"start": v(51.46, -62.35) * mm, "end": v(49.1, -64.2) * mm, "construction": true});
            skLineSegment(sketch, "E19.74.1", {"start": v(49.1, -64.2) * mm, "end": v(46.62, -61.07) * mm, "construction": true});
            skLineSegment(sketch, "E19.74.2", {"start": v(48.98, -59.2) * mm, "end": v(46.62, -61.07) * mm, "construction": true});
            skLineSegment(sketch, "E19.74.3", {"start": v(51.46, -62.35) * mm, "end": v(48.98, -59.2) * mm, "construction": true});
            skLineSegment(sketch, "E19.75.0", {"start": v(54.6, -59.61) * mm, "end": v(52.35, -61.6) * mm, "construction": true});
            skLineSegment(sketch, "E19.75.1", {"start": v(52.35, -61.6) * mm, "end": v(49.7, -58.6) * mm, "construction": true});
            skLineSegment(sketch, "E19.75.2", {"start": v(51.96, -56.6) * mm, "end": v(49.7, -58.6) * mm, "construction": true});
            skLineSegment(sketch, "E19.75.3", {"start": v(54.6, -59.61) * mm, "end": v(51.96, -56.6) * mm, "construction": true});
            skLineSegment(sketch, "E19.76.0", {"start": v(57.6, -56.72) * mm, "end": v(55.45, -58.82) * mm, "construction": true});
            skLineSegment(sketch, "E19.76.1", {"start": v(55.45, -58.82) * mm, "end": v(52.66, -55.95) * mm, "construction": true});
            skLineSegment(sketch, "E19.76.2", {"start": v(54.8, -53.86) * mm, "end": v(52.66, -55.95) * mm, "construction": true});
            skLineSegment(sketch, "E19.76.3", {"start": v(57.6, -56.72) * mm, "end": v(54.8, -53.86) * mm, "construction": true});
            skLineSegment(sketch, "E19.77.0", {"start": v(60.44, -53.68) * mm, "end": v(58.4, -55.89) * mm, "construction": true});
            skLineSegment(sketch, "E19.77.1", {"start": v(58.4, -55.89) * mm, "end": v(55.47, -53.17) * mm, "construction": true});
            skLineSegment(sketch, "E19.77.2", {"start": v(57.5, -50.97) * mm, "end": v(55.47, -53.17) * mm, "construction": true});
            skLineSegment(sketch, "E19.77.3", {"start": v(60.44, -53.68) * mm, "end": v(57.5, -50.97) * mm, "construction": true});
            skLineSegment(sketch, "E19.78.0", {"start": v(63.12, -50.5) * mm, "end": v(61.2, -52.8) * mm, "construction": true});
            skLineSegment(sketch, "E19.78.1", {"start": v(61.2, -52.8) * mm, "end": v(58.13, -50.24) * mm, "construction": true});
            skLineSegment(sketch, "E19.78.2", {"start": v(60.05, -47.94) * mm, "end": v(58.13, -50.24) * mm, "construction": true});
            skLineSegment(sketch, "E19.78.3", {"start": v(63.12, -50.5) * mm, "end": v(60.05, -47.94) * mm, "construction": true});
            skLineSegment(sketch, "E19.79.0", {"start": v(65.64, -47.19) * mm, "end": v(63.84, -49.58) * mm, "construction": true});
            skLineSegment(sketch, "E19.79.1", {"start": v(63.84, -49.58) * mm, "end": v(60.64, -47.18) * mm, "construction": true});
            skLineSegment(sketch, "E19.79.2", {"start": v(62.44, -44.78) * mm, "end": v(60.64, -47.18) * mm, "construction": true});
            skLineSegment(sketch, "E19.79.3", {"start": v(65.64, -47.19) * mm, "end": v(62.44, -44.78) * mm, "construction": true});
            skLineSegment(sketch, "E19.80.0", {"start": v(67.98, -43.74) * mm, "end": v(66.3, -46.23) * mm, "construction": true});
            skLineSegment(sketch, "E19.80.1", {"start": v(66.3, -46.23) * mm, "end": v(62.99, -44) * mm, "construction": true});
            skLineSegment(sketch, "E19.80.2", {"start": v(64.66, -41.51) * mm, "end": v(62.99, -44) * mm, "construction": true});
            skLineSegment(sketch, "E19.80.3", {"start": v(67.98, -43.74) * mm, "end": v(64.66, -41.51) * mm, "construction": true});
            skLineSegment(sketch, "E19.81.0", {"start": v(70.14, -40.19) * mm, "end": v(68.6, -42.76) * mm, "construction": true});
            skLineSegment(sketch, "E19.81.1", {"start": v(68.6, -42.76) * mm, "end": v(65.17, -40.7) * mm, "construction": true});
            skLineSegment(sketch, "E19.81.2", {"start": v(66.71, -38.13) * mm, "end": v(65.17, -40.7) * mm, "construction": true});
            skLineSegment(sketch, "E19.81.3", {"start": v(70.14, -40.19) * mm, "end": v(66.71, -38.13) * mm, "construction": true});
            skLineSegment(sketch, "E19.82.0", {"start": v(72.12, -36.52) * mm, "end": v(70.7, -39.17) * mm, "construction": true});
            skLineSegment(sketch, "E19.82.1", {"start": v(70.7, -39.17) * mm, "end": v(67.18, -37.3) * mm, "construction": true});
            skLineSegment(sketch, "E19.82.2", {"start": v(68.59, -34.64) * mm, "end": v(67.18, -37.3) * mm, "construction": true});
            skLineSegment(sketch, "E19.82.3", {"start": v(72.12, -36.52) * mm, "end": v(68.59, -34.64) * mm, "construction": true});
            skLineSegment(sketch, "E19.83.0", {"start": v(73.9, -32.76) * mm, "end": v(72.63, -35.48) * mm, "construction": true});
            skLineSegment(sketch, "E19.83.1", {"start": v(72.63, -35.48) * mm, "end": v(69, -33.78) * mm, "construction": true});
            skLineSegment(sketch, "E19.83.2", {"start": v(70.28, -31.07) * mm, "end": v(69, -33.78) * mm, "construction": true});
            skLineSegment(sketch, "E19.83.3", {"start": v(73.9, -32.76) * mm, "end": v(70.28, -31.07) * mm, "construction": true});
            skLineSegment(sketch, "E19.84.0", {"start": v(75.5, -28.91) * mm, "end": v(74.36, -31.7) * mm, "construction": true});
            skLineSegment(sketch, "E19.84.1", {"start": v(74.36, -31.7) * mm, "end": v(70.66, -30.19) * mm, "construction": true});
            skLineSegment(sketch, "E19.84.2", {"start": v(71.79, -27.4) * mm, "end": v(70.66, -30.19) * mm, "construction": true});
            skLineSegment(sketch, "E19.84.3", {"start": v(75.5, -28.91) * mm, "end": v(71.79, -27.4) * mm, "construction": true});
            skLineSegment(sketch, "E19.85.0", {"start": v(76.88, -24.99) * mm, "end": v(75.9, -27.82) * mm, "construction": true});
            skLineSegment(sketch, "E19.85.1", {"start": v(75.9, -27.82) * mm, "end": v(72.12, -26.5) * mm, "construction": true});
            skLineSegment(sketch, "E19.85.2", {"start": v(73.1, -23.67) * mm, "end": v(72.12, -26.5) * mm, "construction": true});
            skLineSegment(sketch, "E19.85.3", {"start": v(76.88, -24.99) * mm, "end": v(73.1, -23.67) * mm, "construction": true});
            skLineSegment(sketch, "E19.86.0", {"start": v(78.07, -21) * mm, "end": v(77.23, -23.88) * mm, "construction": true});
            skLineSegment(sketch, "E19.86.1", {"start": v(77.23, -23.88) * mm, "end": v(73.39, -22.76) * mm, "construction": true});
            skLineSegment(sketch, "E19.86.2", {"start": v(74.22, -19.88) * mm, "end": v(73.39, -22.76) * mm, "construction": true});
            skLineSegment(sketch, "E19.86.3", {"start": v(78.07, -21) * mm, "end": v(74.22, -19.88) * mm, "construction": true});
            skLineSegment(sketch, "E19.87.0", {"start": v(79.04, -16.95) * mm, "end": v(78.35, -19.87) * mm, "construction": true});
            skLineSegment(sketch, "E19.87.1", {"start": v(78.35, -19.87) * mm, "end": v(74.46, -18.95) * mm, "construction": true});
            skLineSegment(sketch, "E19.87.2", {"start": v(75.15, -16.03) * mm, "end": v(74.46, -18.95) * mm, "construction": true});
            skLineSegment(sketch, "E19.87.3", {"start": v(79.04, -16.95) * mm, "end": v(75.15, -16.03) * mm, "construction": true});
            skLineSegment(sketch, "E19.88.0", {"start": v(79.81, -12.86) * mm, "end": v(79.27, -15.81) * mm, "construction": true});
            skLineSegment(sketch, "E19.88.1", {"start": v(79.27, -15.81) * mm, "end": v(75.34, -15.1) * mm, "construction": true});
            skLineSegment(sketch, "E19.88.2", {"start": v(75.88, -12.14) * mm, "end": v(75.34, -15.1) * mm, "construction": true});
            skLineSegment(sketch, "E19.88.3", {"start": v(79.81, -12.86) * mm, "end": v(75.88, -12.14) * mm, "construction": true});
            skLineSegment(sketch, "E19.89.0", {"start": v(80.37, -8.73) * mm, "end": v(79.98, -11.7) * mm, "construction": true});
            skLineSegment(sketch, "E19.89.1", {"start": v(79.98, -11.7) * mm, "end": v(76.01, -11.2) * mm, "construction": true});
            skLineSegment(sketch, "E19.89.2", {"start": v(76.4, -8.22) * mm, "end": v(76.01, -11.2) * mm, "construction": true});
            skLineSegment(sketch, "E19.89.3", {"start": v(80.37, -8.73) * mm, "end": v(76.4, -8.22) * mm, "construction": true});
            skLineSegment(sketch, "E19.90.0", {"start": v(80.7, -4.59) * mm, "end": v(80.48, -7.58) * mm, "construction": true});
            skLineSegment(sketch, "E19.90.1", {"start": v(80.48, -7.58) * mm, "end": v(76.49, -7.27) * mm, "construction": true});
            skLineSegment(sketch, "E19.90.2", {"start": v(76.72, -4.28) * mm, "end": v(76.49, -7.27) * mm, "construction": true});
            skLineSegment(sketch, "E19.90.3", {"start": v(80.7, -4.59) * mm, "end": v(76.72, -4.28) * mm, "construction": true});
            skLineSegment(sketch, "E19.91.0", {"start": v(80.84, -0.42) * mm, "end": v(80.76, -3.42) * mm, "construction": true});
            skLineSegment(sketch, "E19.91.1", {"start": v(80.76, -3.42) * mm, "end": v(76.76, -3.32) * mm, "construction": true});
            skLineSegment(sketch, "E19.91.2", {"start": v(76.84, -0.32) * mm, "end": v(76.76, -3.32) * mm, "construction": true});
            skLineSegment(sketch, "E19.91.3", {"start": v(80.84, -0.42) * mm, "end": v(76.84, -0.32) * mm, "construction": true});
            skLineSegment(sketch, "E19.92.0", {"start": v(80.75, 3.74) * mm, "end": v(80.83, 0.74) * mm, "construction": true});
            skLineSegment(sketch, "E19.92.1", {"start": v(80.83, 0.74) * mm, "end": v(76.83, 0.64) * mm, "construction": true});
            skLineSegment(sketch, "E19.92.2", {"start": v(76.75, 3.63) * mm, "end": v(76.83, 0.64) * mm, "construction": true});
            skLineSegment(sketch, "E19.92.3", {"start": v(80.75, 3.74) * mm, "end": v(76.75, 3.63) * mm, "construction": true});
            skLineSegment(sketch, "E19.93.0", {"start": v(80.45, 7.89) * mm, "end": v(80.69, 4.9) * mm, "construction": true});
            skLineSegment(sketch, "E19.93.1", {"start": v(80.69, 4.9) * mm, "end": v(76.7, 4.6) * mm, "construction": true});
            skLineSegment(sketch, "E19.93.2", {"start": v(76.47, 7.58) * mm, "end": v(76.7, 4.6) * mm, "construction": true});
            skLineSegment(sketch, "E19.93.3", {"start": v(80.45, 7.89) * mm, "end": v(76.47, 7.58) * mm, "construction": true});
            skLineSegment(sketch, "E19.94.0", {"start": v(79.94, 12.02) * mm, "end": v(80.33, 9.05) * mm, "construction": true});
            skLineSegment(sketch, "E19.94.1", {"start": v(80.33, 9.05) * mm, "end": v(76.36, 8.53) * mm, "construction": true});
            skLineSegment(sketch, "E19.94.2", {"start": v(75.97, 11.5) * mm, "end": v(76.36, 8.53) * mm, "construction": true});
            skLineSegment(sketch, "E19.94.3", {"start": v(79.94, 12.02) * mm, "end": v(75.97, 11.5) * mm, "construction": true});
            skLineSegment(sketch, "E19.95.0", {"start": v(79.22, 16.12) * mm, "end": v(79.75, 13.17) * mm, "construction": true});
            skLineSegment(sketch, "E19.95.1", {"start": v(79.75, 13.17) * mm, "end": v(75.82, 12.45) * mm, "construction": true});
            skLineSegment(sketch, "E19.95.2", {"start": v(75.28, 15.4) * mm, "end": v(75.82, 12.45) * mm, "construction": true});
            skLineSegment(sketch, "E19.95.3", {"start": v(79.22, 16.12) * mm, "end": v(75.28, 15.4) * mm, "construction": true});
            skLineSegment(sketch, "E19.96.0", {"start": v(78.28, 20.18) * mm, "end": v(78.97, 17.26) * mm, "construction": true});
            skLineSegment(sketch, "E19.96.1", {"start": v(78.97, 17.26) * mm, "end": v(75.08, 16.34) * mm, "construction": true});
            skLineSegment(sketch, "E19.96.2", {"start": v(74.39, 19.26) * mm, "end": v(75.08, 16.34) * mm, "construction": true});
            skLineSegment(sketch, "E19.96.3", {"start": v(78.28, 20.18) * mm, "end": v(74.39, 19.26) * mm, "construction": true});
            skLineSegment(sketch, "E19.97.0", {"start": v(77.14, 24.18) * mm, "end": v(77.98, 21.3) * mm, "construction": true});
            skLineSegment(sketch, "E19.97.1", {"start": v(77.98, 21.3) * mm, "end": v(74.14, 20.18) * mm, "construction": true});
            skLineSegment(sketch, "E19.97.2", {"start": v(73.3, 23.06) * mm, "end": v(74.14, 20.18) * mm, "construction": true});
            skLineSegment(sketch, "E19.97.3", {"start": v(77.14, 24.18) * mm, "end": v(73.3, 23.06) * mm, "construction": true});
            skLineSegment(sketch, "E19.98.0", {"start": v(75.8, 28.12) * mm, "end": v(76.78, 25.29) * mm, "construction": true});
            skLineSegment(sketch, "E19.98.1", {"start": v(76.78, 25.29) * mm, "end": v(73, 23.97) * mm, "construction": true});
            skLineSegment(sketch, "E19.98.2", {"start": v(72.01, 26.8) * mm, "end": v(73, 23.97) * mm, "construction": true});
            skLineSegment(sketch, "E19.98.3", {"start": v(75.8, 28.12) * mm, "end": v(72.01, 26.8) * mm, "construction": true});
            skLineSegment(sketch, "E19.99.0", {"start": v(74.24, 31.98) * mm, "end": v(75.37, 29.2) * mm, "construction": true});
            skLineSegment(sketch, "E19.99.1", {"start": v(75.37, 29.2) * mm, "end": v(71.67, 27.7) * mm, "construction": true});
            skLineSegment(sketch, "E19.99.2", {"start": v(70.54, 30.48) * mm, "end": v(71.67, 27.7) * mm, "construction": true});
            skLineSegment(sketch, "E19.99.3", {"start": v(74.24, 31.98) * mm, "end": v(70.54, 30.48) * mm, "construction": true});
            skLineSegment(sketch, "E19.100.0", {"start": v(72.5, 35.76) * mm, "end": v(73.77, 33.05) * mm, "construction": true});
            skLineSegment(sketch, "E19.100.1", {"start": v(73.77, 33.05) * mm, "end": v(70.15, 31.35) * mm, "construction": true});
            skLineSegment(sketch, "E19.100.2", {"start": v(68.88, 34.07) * mm, "end": v(70.15, 31.35) * mm, "construction": true});
            skLineSegment(sketch, "E19.100.3", {"start": v(72.5, 35.76) * mm, "end": v(68.88, 34.07) * mm, "construction": true});
            skLineSegment(sketch, "E19.101.0", {"start": v(70.56, 39.45) * mm, "end": v(71.97, 36.8) * mm, "construction": true});
            skLineSegment(sketch, "E19.101.1", {"start": v(71.97, 36.8) * mm, "end": v(68.44, 34.92) * mm, "construction": true});
            skLineSegment(sketch, "E19.101.2", {"start": v(67.03, 37.57) * mm, "end": v(68.44, 34.92) * mm, "construction": true});
            skLineSegment(sketch, "E19.101.3", {"start": v(70.56, 39.45) * mm, "end": v(67.03, 37.57) * mm, "construction": true});
            skLineSegment(sketch, "E19.102.0", {"start": v(68.44, 43.03) * mm, "end": v(69.98, 40.46) * mm, "construction": true});
            skLineSegment(sketch, "E19.102.1", {"start": v(69.98, 40.46) * mm, "end": v(66.55, 38.4) * mm, "construction": true});
            skLineSegment(sketch, "E19.102.2", {"start": v(65, 40.97) * mm, "end": v(66.55, 38.4) * mm, "construction": true});
            skLineSegment(sketch, "E19.102.3", {"start": v(68.44, 43.03) * mm, "end": v(65, 40.97) * mm, "construction": true});
            skLineSegment(sketch, "E19.103.0", {"start": v(66.13, 46.5) * mm, "end": v(67.8, 44) * mm, "construction": true});
            skLineSegment(sketch, "E19.103.1", {"start": v(67.8, 44) * mm, "end": v(64.49, 41.77) * mm, "construction": true});
            skLineSegment(sketch, "E19.103.2", {"start": v(62.81, 44.26) * mm, "end": v(64.49, 41.77) * mm, "construction": true});
            skLineSegment(sketch, "E19.103.3", {"start": v(66.13, 46.5) * mm, "end": v(62.81, 44.26) * mm, "construction": true});
            skLineSegment(sketch, "E19.104.0", {"start": v(63.65, 49.84) * mm, "end": v(65.45, 47.44) * mm, "construction": true});
            skLineSegment(sketch, "E19.104.1", {"start": v(65.45, 47.44) * mm, "end": v(62.25, 45.04) * mm, "construction": true});
            skLineSegment(sketch, "E19.104.2", {"start": v(60.45, 47.44) * mm, "end": v(62.25, 45.04) * mm, "construction": true});
            skLineSegment(sketch, "E19.104.3", {"start": v(63.65, 49.84) * mm, "end": v(60.45, 47.44) * mm, "construction": true});
            skLineSegment(sketch, "E19.105.0", {"start": v(61, 53.05) * mm, "end": v(62.92, 50.74) * mm, "construction": true});
            skLineSegment(sketch, "E19.105.1", {"start": v(62.92, 50.74) * mm, "end": v(59.85, 48.18) * mm, "construction": true});
            skLineSegment(sketch, "E19.105.2", {"start": v(57.93, 50.48) * mm, "end": v(59.85, 48.18) * mm, "construction": true});
            skLineSegment(sketch, "E19.105.3", {"start": v(61, 53.05) * mm, "end": v(57.93, 50.48) * mm, "construction": true});
            skLineSegment(sketch, "E19.106.0", {"start": v(58.19, 56.12) * mm, "end": v(60.23, 53.92) * mm, "construction": true});
            skLineSegment(sketch, "E19.106.1", {"start": v(60.23, 53.92) * mm, "end": v(57.3, 51.2) * mm, "construction": true});
            skLineSegment(sketch, "E19.106.2", {"start": v(55.25, 53.4) * mm, "end": v(57.3, 51.2) * mm, "construction": true});
            skLineSegment(sketch, "E19.106.3", {"start": v(58.19, 56.12) * mm, "end": v(55.25, 53.4) * mm, "construction": true});
            skLineSegment(sketch, "E19.107.0", {"start": v(55.22, 59.04) * mm, "end": v(57.37, 56.94) * mm, "construction": true});
            skLineSegment(sketch, "E19.107.1", {"start": v(57.37, 56.94) * mm, "end": v(54.58, 54.08) * mm, "construction": true});
            skLineSegment(sketch, "E19.107.2", {"start": v(52.43, 56.17) * mm, "end": v(54.58, 54.08) * mm, "construction": true});
            skLineSegment(sketch, "E19.107.3", {"start": v(55.22, 59.04) * mm, "end": v(52.43, 56.17) * mm, "construction": true});
            skLineSegment(sketch, "E19.108.0", {"start": v(52.11, 61.8) * mm, "end": v(54.36, 59.82) * mm, "construction": true});
            skLineSegment(sketch, "E19.108.1", {"start": v(54.36, 59.82) * mm, "end": v(51.72, 56.82) * mm, "construction": true});
            skLineSegment(sketch, "E19.108.2", {"start": v(49.47, 58.8) * mm, "end": v(51.72, 56.82) * mm, "construction": true});
            skLineSegment(sketch, "E19.108.3", {"start": v(52.11, 61.8) * mm, "end": v(49.47, 58.8) * mm, "construction": true});
            skLineSegment(sketch, "E19.109.0", {"start": v(48.86, 64.4) * mm, "end": v(51.21, 62.54) * mm, "construction": true});
            skLineSegment(sketch, "E19.109.1", {"start": v(51.21, 62.54) * mm, "end": v(48.73, 59.4) * mm, "construction": true});
            skLineSegment(sketch, "E19.109.2", {"start": v(46.38, 61.27) * mm, "end": v(48.73, 59.4) * mm, "construction": true});
            skLineSegment(sketch, "E19.109.3", {"start": v(48.86, 64.4) * mm, "end": v(46.38, 61.27) * mm, "construction": true});
            skLineSegment(sketch, "E19.110.0", {"start": v(45.48, 66.83) * mm, "end": v(47.92, 65.1) * mm, "construction": true});
            skLineSegment(sketch, "E19.110.1", {"start": v(47.92, 65.1) * mm, "end": v(45.6, 61.83) * mm, "construction": true});
            skLineSegment(sketch, "E19.110.2", {"start": v(43.16, 63.57) * mm, "end": v(45.6, 61.83) * mm, "construction": true});
            skLineSegment(sketch, "E19.110.3", {"start": v(45.48, 66.83) * mm, "end": v(43.16, 63.57) * mm, "construction": true});
            skLineSegment(sketch, "E19.111.0", {"start": v(41.98, 69.09) * mm, "end": v(44.51, 67.48) * mm, "construction": true});
            skLineSegment(sketch, "E19.111.1", {"start": v(44.51, 67.48) * mm, "end": v(42.36, 64.1) * mm, "construction": true});
            skLineSegment(sketch, "E19.111.2", {"start": v(39.83, 65.71) * mm, "end": v(42.36, 64.1) * mm, "construction": true});
            skLineSegment(sketch, "E19.111.3", {"start": v(41.98, 69.09) * mm, "end": v(39.83, 65.71) * mm, "construction": true});
            skLineSegment(sketch, "E19.112.0", {"start": v(38.37, 71.16) * mm, "end": v(40.98, 69.68) * mm, "construction": true});
            skLineSegment(sketch, "E19.112.1", {"start": v(40.98, 69.68) * mm, "end": v(39, 66.2) * mm, "construction": true});
            skLineSegment(sketch, "E19.112.2", {"start": v(36.4, 67.67) * mm, "end": v(39, 66.2) * mm, "construction": true});
            skLineSegment(sketch, "E19.112.3", {"start": v(38.37, 71.16) * mm, "end": v(36.4, 67.67) * mm, "construction": true});
            skLineSegment(sketch, "E19.113.0", {"start": v(34.65, 73.04) * mm, "end": v(37.34, 71.7) * mm, "construction": true});
            skLineSegment(sketch, "E19.113.1", {"start": v(37.34, 71.7) * mm, "end": v(35.55, 68.12) * mm, "construction": true});
            skLineSegment(sketch, "E19.113.2", {"start": v(32.86, 69.46) * mm, "end": v(35.55, 68.12) * mm, "construction": true});
            skLineSegment(sketch, "E19.113.3", {"start": v(34.65, 73.04) * mm, "end": v(32.86, 69.46) * mm, "construction": true});
            skLineSegment(sketch, "E19.114.0", {"start": v(30.85, 74.72) * mm, "end": v(33.6, 73.52) * mm, "construction": true});
            skLineSegment(sketch, "E19.114.1", {"start": v(33.6, 73.52) * mm, "end": v(32, 69.86) * mm, "construction": true});
            skLineSegment(sketch, "E19.114.2", {"start": v(29.25, 71.06) * mm, "end": v(32, 69.86) * mm, "construction": true});
            skLineSegment(sketch, "E19.114.3", {"start": v(30.85, 74.72) * mm, "end": v(29.25, 71.06) * mm, "construction": true});
            skLineSegment(sketch, "E19.115.0", {"start": v(26.96, 76.21) * mm, "end": v(29.77, 75.15) * mm, "construction": true});
            skLineSegment(sketch, "E19.115.1", {"start": v(29.77, 75.15) * mm, "end": v(28.36, 71.41) * mm, "construction": true});
            skLineSegment(sketch, "E19.115.2", {"start": v(25.55, 72.47) * mm, "end": v(28.36, 71.41) * mm, "construction": true});
            skLineSegment(sketch, "E19.115.3", {"start": v(26.96, 76.21) * mm, "end": v(25.55, 72.47) * mm, "construction": true});
            skLineSegment(sketch, "E19.116.0", {"start": v(23, 77.5) * mm, "end": v(25.86, 76.59) * mm, "construction": true});
            skLineSegment(sketch, "E19.116.1", {"start": v(25.86, 76.59) * mm, "end": v(24.64, 72.78) * mm, "construction": true});
            skLineSegment(sketch, "E19.116.2", {"start": v(21.78, 73.69) * mm, "end": v(24.64, 72.78) * mm, "construction": true});
            skLineSegment(sketch, "E19.116.3", {"start": v(23, 77.5) * mm, "end": v(21.78, 73.69) * mm, "construction": true});
            skLineSegment(sketch, "E19.117.0", {"start": v(18.98, 78.58) * mm, "end": v(21.88, 77.82) * mm, "construction": true});
            skLineSegment(sketch, "E19.117.1", {"start": v(21.88, 77.82) * mm, "end": v(20.86, 73.95) * mm, "construction": true});
            skLineSegment(sketch, "E19.117.2", {"start": v(17.96, 74.71) * mm, "end": v(20.86, 73.95) * mm, "construction": true});
            skLineSegment(sketch, "E19.117.3", {"start": v(18.98, 78.58) * mm, "end": v(17.96, 74.71) * mm, "construction": true});
            skLineSegment(sketch, "E19.118.0", {"start": v(14.91, 79.45) * mm, "end": v(17.85, 78.84) * mm, "construction": true});
            skLineSegment(sketch, "E19.118.1", {"start": v(17.85, 78.84) * mm, "end": v(17.03, 74.92) * mm, "construction": true});
            skLineSegment(sketch, "E19.118.2", {"start": v(14.1, 75.54) * mm, "end": v(17.03, 74.92) * mm, "construction": true});
            skLineSegment(sketch, "E19.118.3", {"start": v(14.91, 79.45) * mm, "end": v(14.1, 75.54) * mm, "construction": true});
            skLineSegment(sketch, "E19.119.0", {"start": v(10.8, 80.11) * mm, "end": v(13.76, 79.65) * mm, "construction": true});
            skLineSegment(sketch, "E19.119.1", {"start": v(13.76, 79.65) * mm, "end": v(13.15, 75.7) * mm, "construction": true});
            skLineSegment(sketch, "E19.119.2", {"start": v(10.18, 76.16) * mm, "end": v(13.15, 75.7) * mm, "construction": true});
            skLineSegment(sketch, "E19.119.3", {"start": v(10.8, 80.11) * mm, "end": v(10.18, 76.16) * mm, "construction": true});
            skLineSegment(sketch, "E19.120.0", {"start": v(6.66, 80.56) * mm, "end": v(9.65, 80.26) * mm, "construction": true});
            skLineSegment(sketch, "E19.120.1", {"start": v(9.65, 80.26) * mm, "end": v(9.23, 76.28) * mm, "construction": true});
            skLineSegment(sketch, "E19.120.2", {"start": v(6.25, 76.59) * mm, "end": v(9.23, 76.28) * mm, "construction": true});
            skLineSegment(sketch, "E19.120.3", {"start": v(6.66, 80.56) * mm, "end": v(6.25, 76.59) * mm, "construction": true});
            skLineSegment(sketch, "E19.121.0", {"start": v(2.5, 80.8) * mm, "end": v(5.5, 80.65) * mm, "construction": true});
            skLineSegment(sketch, "E19.121.1", {"start": v(5.5, 80.65) * mm, "end": v(5.3, 76.65) * mm, "construction": true});
            skLineSegment(sketch, "E19.121.2", {"start": v(2.3, 76.8) * mm, "end": v(5.3, 76.65) * mm, "construction": true});
            skLineSegment(sketch, "E19.121.3", {"start": v(2.5, 80.8) * mm, "end": v(2.3, 76.8) * mm, "construction": true});
            skPoint(sketch, "E19.center", {"position": v(0, 0) * mm});
            skSolve(sketch);
        }
        {
            var Q0;
            Q0=makeQuery(id+"F2.imprint","IMPRINT",FACE,{"disambiguationData":[TD([[makeQuery(id+"F2.imprint","IMPRINT",EDGE,{"derivedFrom":makeQuery(id+"F1.opRevolve","SWEPT_EDGE",EDGE,{"disambiguationData":[OSD([sQuery(id+"F0.wireOp",EDGE,"E15.top"),sQuery(id+"F0.wireOp",EDGE,"E15.left")])]})}),1.0]])]});
            var sketch = newSketch(context, id + "F3", { "sketchPlane" : qUnion([Q0])});
            skText(sketch, "E20", { "text": "a", "fontName": "OpenSans-Regular.ttf"});
            skLineSegment(sketch, "E21", {"start": v(0, 0) * mm, "end": v(116.2, 0) * mm, "construction": true});
            skLineSegment(sketch, "E22.1.0", {"start": v(0, 0) * mm, "end": v(116.05, 5.98) * mm, "construction": true});
            skLineSegment(sketch, "E22.2.0", {"start": v(0, 0) * mm, "end": v(115.59, 11.95) * mm, "construction": true});
            skLineSegment(sketch, "E22.3.0", {"start": v(0, 0) * mm, "end": v(114.82, 17.88) * mm, "construction": true});
            skLineSegment(sketch, "E22.4.0", {"start": v(0, 0) * mm, "end": v(113.74, 23.77) * mm, "construction": true});
            skLineSegment(sketch, "E22.5.0", {"start": v(0, 0) * mm, "end": v(112.37, 29.6) * mm, "construction": true});
            skLineSegment(sketch, "E22.6.0", {"start": v(0, 0) * mm, "end": v(110.7, 35.34) * mm, "construction": true});
            skLineSegment(sketch, "E22.7.0", {"start": v(0, 0) * mm, "end": v(108.73, 41) * mm, "construction": true});
            skLineSegment(sketch, "E22.8.0", {"start": v(0, 0) * mm, "end": v(106.48, 46.53) * mm, "construction": true});
            skLineSegment(sketch, "E22.9.0", {"start": v(0, 0) * mm, "end": v(103.94, 51.95) * mm, "construction": true});
            skLineSegment(sketch, "E22.10.0", {"start": v(0, 0) * mm, "end": v(101.13, 57.23) * mm, "construction": true});
            skLineSegment(sketch, "E22.11.0", {"start": v(0, 0) * mm, "end": v(98.05, 62.36) * mm, "construction": true});
            skLineSegment(sketch, "E22.12.0", {"start": v(0, 0) * mm, "end": v(94.7, 67.33) * mm, "construction": true});
            skLineSegment(sketch, "E22.13.0", {"start": v(0, 0) * mm, "end": v(91.12, 72.12) * mm, "construction": true});
            skLineSegment(sketch, "E22.14.0", {"start": v(0, 0) * mm, "end": v(87.28, 76.71) * mm, "construction": true});
            skLineSegment(sketch, "E22.15.0", {"start": v(0, 0) * mm, "end": v(83.22, 81.1) * mm, "construction": true});
            skLineSegment(sketch, "E22.16.0", {"start": v(0, 0) * mm, "end": v(78.93, 85.28) * mm, "construction": true});
            skLineSegment(sketch, "E22.17.0", {"start": v(0, 0) * mm, "end": v(74.44, 89.23) * mm, "construction": true});
            skLineSegment(sketch, "E22.18.0", {"start": v(0, 0) * mm, "end": v(69.75, 92.94) * mm, "construction": true});
            skLineSegment(sketch, "E22.19.0", {"start": v(0, 0) * mm, "end": v(64.87, 96.4) * mm, "construction": true});
            skLineSegment(sketch, "E22.20.0", {"start": v(0, 0) * mm, "end": v(59.82, 99.62) * mm, "construction": true});
            skLineSegment(sketch, "E22.21.0", {"start": v(0, 0) * mm, "end": v(54.61, 102.57) * mm, "construction": true});
            skLineSegment(sketch, "E22.22.0", {"start": v(0, 0) * mm, "end": v(49.26, 105.24) * mm, "construction": true});
            skLineSegment(sketch, "E22.23.0", {"start": v(0, 0) * mm, "end": v(43.78, 107.64) * mm, "construction": true});
            skLineSegment(sketch, "E22.24.0", {"start": v(0, 0) * mm, "end": v(38.18, 109.75) * mm, "construction": true});
            skLineSegment(sketch, "E22.25.0", {"start": v(0, 0) * mm, "end": v(32.48, 111.57) * mm, "construction": true});
            skLineSegment(sketch, "E22.26.0", {"start": v(0, 0) * mm, "end": v(26.7, 113.1) * mm, "construction": true});
            skLineSegment(sketch, "E22.27.0", {"start": v(0, 0) * mm, "end": v(20.83, 114.32) * mm, "construction": true});
            skLineSegment(sketch, "E22.28.0", {"start": v(0, 0) * mm, "end": v(14.92, 115.24) * mm, "construction": true});
            skLineSegment(sketch, "E22.29.0", {"start": v(0, 0) * mm, "end": v(8.97, 115.85) * mm, "construction": true});
            skLineSegment(sketch, "E22.30.0", {"start": v(0, 0) * mm, "end": v(3, 116.16) * mm, "construction": true});
            skLineSegment(sketch, "E22.31.0", {"start": v(0, 0) * mm, "end": v(-3, 116.16) * mm, "construction": true});
            skLineSegment(sketch, "E22.32.0", {"start": v(0, 0) * mm, "end": v(-8.97, 115.85) * mm, "construction": true});
            skLineSegment(sketch, "E22.33.0", {"start": v(0, 0) * mm, "end": v(-14.92, 115.24) * mm, "construction": true});
            skLineSegment(sketch, "E22.34.0", {"start": v(0, 0) * mm, "end": v(-20.83, 114.32) * mm, "construction": true});
            skLineSegment(sketch, "E22.35.0", {"start": v(0, 0) * mm, "end": v(-26.7, 113.1) * mm, "construction": true});
            skLineSegment(sketch, "E22.36.0", {"start": v(0, 0) * mm, "end": v(-32.48, 111.57) * mm, "construction": true});
            skLineSegment(sketch, "E22.37.0", {"start": v(0, 0) * mm, "end": v(-38.18, 109.75) * mm, "construction": true});
            skLineSegment(sketch, "E22.38.0", {"start": v(0, 0) * mm, "end": v(-43.78, 107.64) * mm, "construction": true});
            skLineSegment(sketch, "E22.39.0", {"start": v(0, 0) * mm, "end": v(-49.26, 105.24) * mm, "construction": true});
            skLineSegment(sketch, "E22.40.0", {"start": v(0, 0) * mm, "end": v(-54.61, 102.57) * mm, "construction": true});
            skLineSegment(sketch, "E22.41.0", {"start": v(0, 0) * mm, "end": v(-59.82, 99.62) * mm, "construction": true});
            skLineSegment(sketch, "E22.42.0", {"start": v(0, 0) * mm, "end": v(-64.87, 96.4) * mm, "construction": true});
            skLineSegment(sketch, "E22.43.0", {"start": v(0, 0) * mm, "end": v(-69.75, 92.94) * mm, "construction": true});
            skLineSegment(sketch, "E22.44.0", {"start": v(0, 0) * mm, "end": v(-74.44, 89.23) * mm, "construction": true});
            skLineSegment(sketch, "E22.45.0", {"start": v(0, 0) * mm, "end": v(-78.93, 85.28) * mm, "construction": true});
            skLineSegment(sketch, "E22.46.0", {"start": v(0, 0) * mm, "end": v(-83.22, 81.1) * mm, "construction": true});
            skLineSegment(sketch, "E22.47.0", {"start": v(0, 0) * mm, "end": v(-87.28, 76.71) * mm, "construction": true});
            skLineSegment(sketch, "E22.48.0", {"start": v(0, 0) * mm, "end": v(-91.12, 72.12) * mm, "construction": true});
            skLineSegment(sketch, "E22.49.0", {"start": v(0, 0) * mm, "end": v(-94.7, 67.33) * mm, "construction": true});
            skLineSegment(sketch, "E22.50.0", {"start": v(0, 0) * mm, "end": v(-98.05, 62.36) * mm, "construction": true});
            skLineSegment(sketch, "E22.51.0", {"start": v(0, 0) * mm, "end": v(-101.13, 57.23) * mm, "construction": true});
            skLineSegment(sketch, "E22.52.0", {"start": v(0, 0) * mm, "end": v(-103.94, 51.95) * mm, "construction": true});
            skLineSegment(sketch, "E22.53.0", {"start": v(0, 0) * mm, "end": v(-106.48, 46.53) * mm, "construction": true});
            skLineSegment(sketch, "E22.54.0", {"start": v(0, 0) * mm, "end": v(-108.73, 41) * mm, "construction": true});
            skLineSegment(sketch, "E22.55.0", {"start": v(0, 0) * mm, "end": v(-110.7, 35.34) * mm, "construction": true});
            skLineSegment(sketch, "E22.56.0", {"start": v(0, 0) * mm, "end": v(-112.37, 29.6) * mm, "construction": true});
            skLineSegment(sketch, "E22.57.0", {"start": v(0, 0) * mm, "end": v(-113.74, 23.77) * mm, "construction": true});
            skLineSegment(sketch, "E22.58.0", {"start": v(0, 0) * mm, "end": v(-114.82, 17.88) * mm, "construction": true});
            skLineSegment(sketch, "E22.59.0", {"start": v(0, 0) * mm, "end": v(-115.59, 11.95) * mm, "construction": true});
            skLineSegment(sketch, "E22.60.0", {"start": v(0, 0) * mm, "end": v(-116.05, 5.98) * mm, "construction": true});
            skLineSegment(sketch, "E22.61.0", {"start": v(0, 0) * mm, "end": v(-116.2, 0) * mm, "construction": true});
            skLineSegment(sketch, "E22.62.0", {"start": v(0, 0) * mm, "end": v(-116.05, -5.98) * mm, "construction": true});
            skLineSegment(sketch, "E22.63.0", {"start": v(0, 0) * mm, "end": v(-115.59, -11.95) * mm, "construction": true});
            skLineSegment(sketch, "E22.64.0", {"start": v(0, 0) * mm, "end": v(-114.82, -17.88) * mm, "construction": true});
            skLineSegment(sketch, "E22.65.0", {"start": v(0, 0) * mm, "end": v(-113.74, -23.77) * mm, "construction": true});
            skLineSegment(sketch, "E22.66.0", {"start": v(0, 0) * mm, "end": v(-112.37, -29.6) * mm, "construction": true});
            skLineSegment(sketch, "E22.67.0", {"start": v(0, 0) * mm, "end": v(-110.7, -35.34) * mm, "construction": true});
            skLineSegment(sketch, "E22.68.0", {"start": v(0, 0) * mm, "end": v(-108.73, -41) * mm, "construction": true});
            skLineSegment(sketch, "E22.69.0", {"start": v(0, 0) * mm, "end": v(-106.48, -46.53) * mm, "construction": true});
            skLineSegment(sketch, "E22.70.0", {"start": v(0, 0) * mm, "end": v(-103.94, -51.95) * mm, "construction": true});
            skLineSegment(sketch, "E22.71.0", {"start": v(0, 0) * mm, "end": v(-101.13, -57.23) * mm, "construction": true});
            skLineSegment(sketch, "E22.72.0", {"start": v(0, 0) * mm, "end": v(-98.05, -62.36) * mm, "construction": true});
            skLineSegment(sketch, "E22.73.0", {"start": v(0, 0) * mm, "end": v(-94.7, -67.33) * mm, "construction": true});
            skLineSegment(sketch, "E22.74.0", {"start": v(0, 0) * mm, "end": v(-91.12, -72.12) * mm, "construction": true});
            skLineSegment(sketch, "E22.75.0", {"start": v(0, 0) * mm, "end": v(-87.28, -76.71) * mm, "construction": true});
            skLineSegment(sketch, "E22.76.0", {"start": v(0, 0) * mm, "end": v(-83.22, -81.1) * mm, "construction": true});
            skLineSegment(sketch, "E22.77.0", {"start": v(0, 0) * mm, "end": v(-78.93, -85.28) * mm, "construction": true});
            skLineSegment(sketch, "E22.78.0", {"start": v(0, 0) * mm, "end": v(-74.44, -89.23) * mm, "construction": true});
            skLineSegment(sketch, "E22.79.0", {"start": v(0, 0) * mm, "end": v(-69.75, -92.94) * mm, "construction": true});
            skLineSegment(sketch, "E22.80.0", {"start": v(0, 0) * mm, "end": v(-64.87, -96.4) * mm, "construction": true});
            skLineSegment(sketch, "E22.81.0", {"start": v(0, 0) * mm, "end": v(-59.82, -99.62) * mm, "construction": true});
            skLineSegment(sketch, "E22.82.0", {"start": v(0, 0) * mm, "end": v(-54.61, -102.57) * mm, "construction": true});
            skLineSegment(sketch, "E22.83.0", {"start": v(0, 0) * mm, "end": v(-49.26, -105.24) * mm, "construction": true});
            skLineSegment(sketch, "E22.84.0", {"start": v(0, 0) * mm, "end": v(-43.78, -107.64) * mm, "construction": true});
            skLineSegment(sketch, "E22.85.0", {"start": v(0, 0) * mm, "end": v(-38.18, -109.75) * mm, "construction": true});
            skLineSegment(sketch, "E22.86.0", {"start": v(0, 0) * mm, "end": v(-32.48, -111.57) * mm, "construction": true});
            skLineSegment(sketch, "E22.87.0", {"start": v(0, 0) * mm, "end": v(-26.7, -113.1) * mm, "construction": true});
            skLineSegment(sketch, "E22.88.0", {"start": v(0, 0) * mm, "end": v(-20.83, -114.32) * mm, "construction": true});
            skLineSegment(sketch, "E22.89.0", {"start": v(0, 0) * mm, "end": v(-14.92, -115.24) * mm, "construction": true});
            skLineSegment(sketch, "E22.90.0", {"start": v(0, 0) * mm, "end": v(-8.97, -115.85) * mm, "construction": true});
            skLineSegment(sketch, "E22.91.0", {"start": v(0, 0) * mm, "end": v(-3, -116.16) * mm, "construction": true});
            skLineSegment(sketch, "E22.92.0", {"start": v(0, 0) * mm, "end": v(3, -116.16) * mm, "construction": true});
            skLineSegment(sketch, "E22.93.0", {"start": v(0, 0) * mm, "end": v(8.97, -115.85) * mm, "construction": true});
            skLineSegment(sketch, "E22.94.0", {"start": v(0, 0) * mm, "end": v(14.92, -115.24) * mm, "construction": true});
            skLineSegment(sketch, "E22.95.0", {"start": v(0, 0) * mm, "end": v(20.83, -114.32) * mm, "construction": true});
            skLineSegment(sketch, "E22.96.0", {"start": v(0, 0) * mm, "end": v(26.7, -113.1) * mm, "construction": true});
            skLineSegment(sketch, "E22.97.0", {"start": v(0, 0) * mm, "end": v(32.48, -111.57) * mm, "construction": true});
            skLineSegment(sketch, "E22.98.0", {"start": v(0, 0) * mm, "end": v(38.18, -109.75) * mm, "construction": true});
            skLineSegment(sketch, "E22.99.0", {"start": v(0, 0) * mm, "end": v(43.78, -107.64) * mm, "construction": true});
            skLineSegment(sketch, "E22.100.0", {"start": v(0, 0) * mm, "end": v(49.26, -105.24) * mm, "construction": true});
            skLineSegment(sketch, "E22.101.0", {"start": v(0, 0) * mm, "end": v(54.61, -102.57) * mm, "construction": true});
            skLineSegment(sketch, "E22.102.0", {"start": v(0, 0) * mm, "end": v(59.82, -99.62) * mm, "construction": true});
            skLineSegment(sketch, "E22.103.0", {"start": v(0, 0) * mm, "end": v(64.87, -96.4) * mm, "construction": true});
            skLineSegment(sketch, "E22.104.0", {"start": v(0, 0) * mm, "end": v(69.75, -92.94) * mm, "construction": true});
            skLineSegment(sketch, "E22.105.0", {"start": v(0, 0) * mm, "end": v(74.44, -89.23) * mm, "construction": true});
            skLineSegment(sketch, "E22.106.0", {"start": v(0, 0) * mm, "end": v(78.93, -85.28) * mm, "construction": true});
            skLineSegment(sketch, "E22.107.0", {"start": v(0, 0) * mm, "end": v(83.22, -81.1) * mm, "construction": true});
            skLineSegment(sketch, "E22.108.0", {"start": v(0, 0) * mm, "end": v(87.28, -76.71) * mm, "construction": true});
            skLineSegment(sketch, "E22.109.0", {"start": v(0, 0) * mm, "end": v(91.12, -72.12) * mm, "construction": true});
            skLineSegment(sketch, "E22.110.0", {"start": v(0, 0) * mm, "end": v(94.7, -67.33) * mm, "construction": true});
            skLineSegment(sketch, "E22.111.0", {"start": v(0, 0) * mm, "end": v(98.05, -62.36) * mm, "construction": true});
            skLineSegment(sketch, "E22.112.0", {"start": v(0, 0) * mm, "end": v(101.13, -57.23) * mm, "construction": true});
            skLineSegment(sketch, "E22.113.0", {"start": v(0, 0) * mm, "end": v(103.94, -51.95) * mm, "construction": true});
            skLineSegment(sketch, "E22.114.0", {"start": v(0, 0) * mm, "end": v(106.48, -46.53) * mm, "construction": true});
            skLineSegment(sketch, "E22.115.0", {"start": v(0, 0) * mm, "end": v(108.73, -41) * mm, "construction": true});
            skLineSegment(sketch, "E22.116.0", {"start": v(0, 0) * mm, "end": v(110.7, -35.34) * mm, "construction": true});
            skLineSegment(sketch, "E22.117.0", {"start": v(0, 0) * mm, "end": v(112.37, -29.6) * mm, "construction": true});
            skLineSegment(sketch, "E22.118.0", {"start": v(0, 0) * mm, "end": v(113.74, -23.77) * mm, "construction": true});
            skLineSegment(sketch, "E22.119.0", {"start": v(0, 0) * mm, "end": v(114.82, -17.88) * mm, "construction": true});
            skLineSegment(sketch, "E22.120.0", {"start": v(0, 0) * mm, "end": v(115.59, -11.95) * mm, "construction": true});
            skLineSegment(sketch, "E22.121.0", {"start": v(0, 0) * mm, "end": v(116.05, -5.98) * mm, "construction": true});
            skPoint(sketch, "E22.center", {"position": v(0, 0) * mm});
            skCircle(sketch, "E23", {"center": v(0, 0) * mm, "radius": 78.75 * mm, "construction": true});
            skText(sketch, "E24", { "text": "m", "fontName": "OpenSans-Regular.ttf"});
            skText(sketch, "E25", { "text": "o", "fontName": "OpenSans-Regular.ttf"});
            skText(sketch, "E26", { "text": "d", "fontName": "OpenSans-Regular.ttf"});
            skText(sketch, "E27", { "text": "e", "fontName": "OpenSans-Regular.ttf"});
            skText(sketch, "E28", { "text": "l", "fontName": "OpenSans-Regular.ttf"});
            skText(sketch, "E29", { "text": "i", "fontName": "OpenSans-Regular.ttf"});
            skText(sketch, "E30", { "text": "s", "fontName": "OpenSans-Regular.ttf"});
            skText(sketch, "E31", { "text": "a", "fontName": "OpenSans-Regular.ttf"});
            skText(sketch, "E32", { "text": "o", "fontName": "OpenSans-Regular.ttf"});
            skText(sketch, "E33", { "text": "p", "fontName": "OpenSans-Regular.ttf"});
            skText(sketch, "E34", { "text": "r", "fontName": "OpenSans-Regular.ttf"});
            skText(sketch, "E35", { "text": "e", "fontName": "OpenSans-Regular.ttf"});
            skText(sketch, "E36", { "text": "r", "fontName": "OpenSans-Regular.ttf"});
            skText(sketch, "E37", { "text": "e", "fontName": "OpenSans-Regular.ttf"});
            skText(sketch, "E38", { "text": "s", "fontName": "OpenSans-Regular.ttf"});
            skText(sketch, "E39", { "text": "n", "fontName": "OpenSans-Regular.ttf"});
            skText(sketch, "E40", { "text": "e", "fontName": "OpenSans-Regular.ttf"});
            skText(sketch, "E41", { "text": "t", "fontName": "OpenSans-Regular.ttf"});
            skText(sketch, "E42", { "text": "a", "fontName": "OpenSans-Regular.ttf"});
            skText(sketch, "E43", { "text": "t", "fontName": "OpenSans-Regular.ttf"});
            skText(sketch, "E44", { "text": "i", "fontName": "OpenSans-Regular.ttf"});
            skText(sketch, "E45", { "text": "o", "fontName": "OpenSans-Regular.ttf"});
            skText(sketch, "E46", { "text": "f", "fontName": "OpenSans-Regular.ttf"});
            skText(sketch, "E47", { "text": "n", "fontName": "OpenSans-Regular.ttf"});
            skText(sketch, "E48", { "text": "r", "fontName": "OpenSans-Regular.ttf"});
            skText(sketch, "E49", { "text": "e", "fontName": "OpenSans-Regular.ttf"});
            skText(sketch, "E50", { "text": "a", "fontName": "OpenSans-Regular.ttf"});
            skText(sketch, "E51", { "text": "l", "fontName": "OpenSans-Regular.ttf"});
            skText(sketch, "E52", { "text": "i", "fontName": "OpenSans-Regular.ttf"});
            skText(sketch, "E53", { "text": "t", "fontName": "OpenSans-Regular.ttf"});
            skText(sketch, "E54", { "text": "y", "fontName": "OpenSans-Regular.ttf"});
            skText(sketch, "E55", { "text": "i", "fontName": "OpenSans-Regular.ttf"});
            skText(sketch, "E56", { "text": "s", "fontName": "OpenSans-Regular.ttf"});
            skText(sketch, "E57", { "text": "a", "fontName": "OpenSans-Regular.ttf"});
            skText(sketch, "E58", { "text": "m", "fontName": "OpenSans-Regular.ttf"});
            skText(sketch, "E59", { "text": "a", "fontName": "OpenSans-Regular.ttf"});
            skText(sketch, "E60", { "text": "n", "fontName": "OpenSans-Regular.ttf"});
            skText(sketch, "E61", { "text": "i", "fontName": "OpenSans-Regular.ttf"});
            skText(sketch, "E62", { "text": "f", "fontName": "OpenSans-Regular.ttf"});
            skText(sketch, "E63", { "text": "e", "fontName": "OpenSans-Regular.ttf"});
            skText(sketch, "E64", { "text": "s", "fontName": "OpenSans-Regular.ttf"});
            skText(sketch, "E65", { "text": "t", "fontName": "OpenSans-Regular.ttf"});
            skText(sketch, "E66", { "text": "a", "fontName": "OpenSans-Regular.ttf"});
            skText(sketch, "E67", { "text": "t", "fontName": "OpenSans-Regular.ttf"});
            skText(sketch, "E68", { "text": "i", "fontName": "OpenSans-Regular.ttf"});
            skText(sketch, "E69", { "text": "o", "fontName": "OpenSans-Regular.ttf"});
            skText(sketch, "E70", { "text": "n", "fontName": "OpenSans-Regular.ttf"});
            skText(sketch, "E71", { "text": "o", "fontName": "OpenSans-Regular.ttf"});
            skText(sketch, "E72", { "text": "f", "fontName": "OpenSans-Regular.ttf"});
            skText(sketch, "E73", { "text": "a", "fontName": "OpenSans-Regular.ttf"});
            skText(sketch, "E74", { "text": "m", "fontName": "OpenSans-Regular.ttf"});
            skText(sketch, "E75", { "text": "o", "fontName": "OpenSans-Regular.ttf"});
            skText(sketch, "E76", { "text": "d", "fontName": "OpenSans-Regular.ttf"});
            skText(sketch, "E77", { "text": "e", "fontName": "OpenSans-Regular.ttf"});
            skText(sketch, "E78", { "text": "l", "fontName": "OpenSans-Regular.ttf"});
            skText(sketch, "E79", { "text": "i", "fontName": "OpenSans-Regular.ttf"});
            skText(sketch, "E80", { "text": "s", "fontName": "OpenSans-Regular.ttf"});
            skText(sketch, "E81", { "text": "a", "fontName": "OpenSans-Regular.ttf"});
            skText(sketch, "E82", { "text": "r", "fontName": "OpenSans-Regular.ttf"});
            skText(sketch, "E83", { "text": "e", "fontName": "OpenSans-Regular.ttf"});
            skText(sketch, "E84", { "text": "p", "fontName": "OpenSans-Regular.ttf"});
            skText(sketch, "E85", { "text": "r", "fontName": "OpenSans-Regular.ttf"});
            skText(sketch, "E86", { "text": "e", "fontName": "OpenSans-Regular.ttf"});
            skText(sketch, "E87", { "text": "s", "fontName": "OpenSans-Regular.ttf"});
            skText(sketch, "E88", { "text": "e", "fontName": "OpenSans-Regular.ttf"});
            skText(sketch, "E89", { "text": "n", "fontName": "OpenSans-Regular.ttf"});
            skText(sketch, "E90", { "text": "t", "fontName": "OpenSans-Regular.ttf"});
            skText(sketch, "E91", { "text": "a", "fontName": "OpenSans-Regular.ttf"});
            skText(sketch, "E92", { "text": "t", "fontName": "OpenSans-Regular.ttf"});
            skText(sketch, "E93", { "text": "i", "fontName": "OpenSans-Regular.ttf"});
            skText(sketch, "E94", { "text": "o", "fontName": "OpenSans-Regular.ttf"});
            skText(sketch, "E95", { "text": "n", "fontName": "OpenSans-Regular.ttf"});
            skText(sketch, "E96", { "text": "o", "fontName": "OpenSans-Regular.ttf"});
            skText(sketch, "E97", { "text": "f", "fontName": "OpenSans-Regular.ttf"});
            skText(sketch, "E98", { "text": "r", "fontName": "OpenSans-Regular.ttf"});
            skText(sketch, "E99", { "text": "e", "fontName": "OpenSans-Regular.ttf"});
            skText(sketch, "E100", { "text": "a", "fontName": "OpenSans-Regular.ttf"});
            skText(sketch, "E101", { "text": "l", "fontName": "OpenSans-Regular.ttf"});
            skText(sketch, "E102", { "text": "i", "fontName": "OpenSans-Regular.ttf"});
            skText(sketch, "E103", { "text": "t", "fontName": "OpenSans-Regular.ttf"});
            skText(sketch, "E104", { "text": "y", "fontName": "OpenSans-Regular.ttf"});
            skText(sketch, "E105", { "text": "i", "fontName": "OpenSans-Regular.ttf"});
            skText(sketch, "E106", { "text": "s", "fontName": "OpenSans-Regular.ttf"});
            skText(sketch, "E107", { "text": "a", "fontName": "OpenSans-Regular.ttf"});
            skText(sketch, "E108", { "text": "m", "fontName": "OpenSans-Regular.ttf"});
            skText(sketch, "E109", { "text": "a", "fontName": "OpenSans-Regular.ttf"});
            skText(sketch, "E110", { "text": "n", "fontName": "OpenSans-Regular.ttf"});
            skText(sketch, "E111", { "text": "i", "fontName": "OpenSans-Regular.ttf"});
            skText(sketch, "E112", { "text": "f", "fontName": "OpenSans-Regular.ttf"});
            skText(sketch, "E113", { "text": "e", "fontName": "OpenSans-Regular.ttf"});
            skText(sketch, "E114", { "text": "s", "fontName": "OpenSans-Regular.ttf"});
            skText(sketch, "E115", { "text": "t", "fontName": "OpenSans-Regular.ttf"});
            skText(sketch, "E116", { "text": "a", "fontName": "OpenSans-Regular.ttf"});
            skText(sketch, "E117", { "text": "t", "fontName": "OpenSans-Regular.ttf"});
            skText(sketch, "E118", { "text": "i", "fontName": "OpenSans-Regular.ttf"});
            skText(sketch, "E119", { "text": "o", "fontName": "OpenSans-Regular.ttf"});
            skText(sketch, "E120", { "text": "n", "fontName": "OpenSans-Regular.ttf"});
            skText(sketch, "E121", { "text": "o", "fontName": "OpenSans-Regular.ttf"});
            skText(sketch, "E122", { "text": "f", "fontName": "OpenSans-Regular.ttf"});
            const initialGuessF3  = {"E20": [0.07875, 0.00169, 0, -1, 0.0045], "E24": [0.07863, -0.00526, -0.10282, -0.9947, 0.0045], "E25": [0.0781, -0.01023, -0.1539, -0.98809, 0.0045], "E26": [0.07746, -0.0143, -0.20455, -0.97886, 0.0045], "E27": [0.0766, -0.01832, -0.25467, -0.96703, 0.0045], "E28": [0.07524, -0.02326, -0.30411, -0.95264, 0.0045], "E29": [0.07246, -0.03085, -0.40045, -0.91632, 0.0045], "E30": [0.07113, -0.03382, -0.4471, -0.89449, 0.0045], "E31": [0.06735, -0.04084, -0.5367, -0.84378, 0.0045], "E32": [0.01201, -0.07785, -0.99172, -0.1284, 0.0045], "E33": [0.05775, -0.05357, -0.69794, -0.71615, 0.0045], "E34": [0.06264, -0.04775, -0.6206, -0.78412, 0.0045], "E35": [0.06033, -0.05064, -0.66015, -0.75113, 0.0045], "E36": [0.05455, -0.05682, -0.73389, -0.67927, 0.0045], "E37": [0.05182, -0.05932, -0.76788, -0.6406, 0.0045], "E38": [0.0485, -0.06206, -0.79984, -0.60021, 0.0045], "E39": [0.04214, -0.06655, -0.85731, -0.5148, 0.0045], "E40": [0.04545, -0.06434, -0.82968, -0.55824, 0.0045], "E41": [0.0381, -0.06893, -0.88268, -0.46998, 0.0045], "E42": [0.03491, -0.0706, -0.9057, -0.42391, 0.0045], "E43": [0.03082, -0.07248, -0.92632, -0.37673, 0.0045], "E44": [0.02658, -0.07413, -0.94449, -0.32854, 0.0045], "E45": [0.02385, -0.07508, -0.96015, -0.27949, 0.0045], "E46": [0.00747, -0.0784, -0.99702, -0.07718, 0.0045], "E47": [0.0199, -0.07622, -0.97326, -0.22969, 0.0045], "E48": [-0.0006, -0.07876, -0.99967, 0.02575, 0.0045], "E49": [-0.0043, -0.07865, -0.99702, 0.07718, 0.0045], "E50": [-0.00844, -0.07831, -0.99172, 0.1284, 0.0045], "E51": [-0.0134, -0.0776, -0.9838, 0.17928, 0.0045], "E52": [-0.01736, -0.07682, -0.97326, 0.22969, 0.0045], "E53": [-0.02082, -0.07596, -0.96015, 0.27949, 0.0045], "E54": [-0.0242, -0.07496, -0.94449, 0.32854, 0.0045], "E55": [-0.0327, -0.07164, -0.9057, 0.42391, 0.0045], "E56": [-0.03564, -0.07024, -0.88268, 0.46998, 0.0045], "E57": [-0.04256, -0.06628, -0.82968, 0.55824, 0.0045], "E58": [-0.04825, -0.0623, -0.76788, 0.6406, 0.0045], "E59": [-0.05225, -0.05894, -0.73389, 0.67927, 0.0045], "E60": [-0.0551, -0.0563, -0.69794, 0.71615, 0.0045], "E61": [-0.05866, -0.05255, -0.66015, 0.75113, 0.0045], "E62": [-0.06088, -0.04997, -0.6206, 0.78412, 0.0045], "E63": [-0.06314, -0.0471, -0.57942, 0.81503, 0.0045], "E64": [-0.06562, -0.04357, -0.5367, 0.84378, 0.0045], "E65": [-0.06792, -0.03987, -0.49255, 0.87029, 0.0045], "E66": [-0.06969, -0.03672, -0.4471, 0.89449, 0.0045], "E67": [-0.07166, -0.03267, -0.40045, 0.91632, 0.0045], "E68": [-0.07342, -0.02848, -0.35275, 0.93572, 0.0045], "E69": [-0.07444, -0.02577, -0.30411, 0.95264, 0.0045], "E70": [-0.07568, -0.02186, -0.25467, 0.96703, 0.0045], "E71": [-0.07752, -0.01401, -0.1539, 0.98809, 0.0045], "E72": [-0.07819, -0.00949, -0.10282, 0.9947, 0.0045], "E73": [-0.07875, -0.00169, 0, 1, 0.0045], "E74": [-0.07863, 0.00526, 0.10282, 0.9947, 0.0045], "E75": [-0.0781, 0.01023, 0.1539, 0.98809, 0.0045], "E76": [-0.07746, 0.0143, 0.20455, 0.97886, 0.0045], "E77": [-0.0766, 0.01832, 0.25467, 0.96703, 0.0045], "E78": [-0.07524, 0.02326, 0.30411, 0.95264, 0.0045], "E79": [-0.07246, 0.03085, 0.40045, 0.91632, 0.0045], "E80": [-0.07113, 0.03382, 0.4471, 0.89449, 0.0045], "E81": [-0.06735, 0.04084, 0.5367, 0.84378, 0.0045], "E82": [-0.06264, 0.04775, 0.6206, 0.78412, 0.0045], "E83": [-0.06033, 0.05064, 0.66015, 0.75113, 0.0045], "E84": [-0.05775, 0.05357, 0.69794, 0.71615, 0.0045], "E85": [-0.05455, 0.05682, 0.73389, 0.67927, 0.0045], "E86": [-0.05182, 0.05932, 0.76788, 0.6406, 0.0045], "E87": [-0.0485, 0.06206, 0.79984, 0.60021, 0.0045], "E88": [-0.04545, 0.06434, 0.82968, 0.55824, 0.0045], "E89": [-0.04214, 0.06655, 0.85731, 0.5148, 0.0045], "E90": [-0.0381, 0.06893, 0.88268, 0.46998, 0.0045], "E91": [-0.03491, 0.0706, 0.9057, 0.42391, 0.0045], "E92": [-0.03082, 0.07248, 0.92632, 0.37673, 0.0045], "E93": [-0.02658, 0.07413, 0.94449, 0.32854, 0.0045], "E94": [-0.02385, 0.07508, 0.96015, 0.27949, 0.0045], "E95": [-0.0199, 0.07622, 0.97326, 0.22969, 0.0045], "E96": [-0.01201, 0.07785, 0.99172, 0.1284, 0.0045], "E97": [-0.00747, 0.0784, 0.99702, 0.07718, 0.0045], "E98": [0.0006, 0.07876, 0.99967, -0.02575, 0.0045], "E99": [0.0043, 0.07865, 0.99702, -0.07718, 0.0045], "E100": [0.00844, 0.07831, 0.99172, -0.1284, 0.0045], "E101": [0.0134, 0.0776, 0.9838, -0.17928, 0.0045], "E102": [0.01736, 0.07682, 0.97326, -0.22969, 0.0045], "E103": [0.02082, 0.07596, 0.96015, -0.27949, 0.0045], "E104": [0.0242, 0.07496, 0.94449, -0.32854, 0.0045], "E105": [0.0327, 0.07164, 0.9057, -0.42391, 0.0045], "E106": [0.03564, 0.07024, 0.88268, -0.46998, 0.0045], "E107": [0.04256, 0.06628, 0.82968, -0.55824, 0.0045], "E108": [0.04825, 0.0623, 0.76788, -0.6406, 0.0045], "E109": [0.05225, 0.05894, 0.73389, -0.67927, 0.0045], "E110": [0.0551, 0.0563, 0.69794, -0.71615, 0.0045], "E111": [0.05866, 0.05255, 0.66015, -0.75113, 0.0045], "E112": [0.06088, 0.04997, 0.6206, -0.78412, 0.0045], "E113": [0.06314, 0.0471, 0.57942, -0.81503, 0.0045], "E114": [0.06562, 0.04357, 0.5367, -0.84378, 0.0045], "E115": [0.06792, 0.03987, 0.49255, -0.87029, 0.0045], "E116": [0.06969, 0.03672, 0.4471, -0.89449, 0.0045], "E117": [0.07166, 0.03267, 0.40045, -0.91632, 0.0045], "E118": [0.07342, 0.02848, 0.35275, -0.93572, 0.0045], "E119": [0.07444, 0.02577, 0.30411, -0.95264, 0.0045], "E120": [0.07568, 0.02186, 0.25467, -0.96703, 0.0045], "E121": [0.07752, 0.01401, 0.1539, -0.98809, 0.0045], "E122": [0.07819, 0.00949, 0.10282, -0.9947, 0.0045]};
            skSetInitialGuess(sketch, initialGuessF3);
            skSolve(sketch);
        }
        {
            var Q0;
            Q0 = qSketchRegion(id + "F3", true);
            extrude(context, id + "F4", {"entities" : qUnion([Q0]), "operationType" : NewBodyOperationType.REMOVE, "oppositeDirection" : true, "depth" : 0.5 * mm});
        }
        {
            var Q0;
            Q0=qCreatedBy(makeId("Top.planeOp"),FACE);
            var sketch = newSketch(context, id + "F5", { "sketchPlane" : qUnion([Q0])});
            skLineSegment(sketch, "E123.bottom", {"start": v(-0.25, 125) * mm, "end": v(0.25, 125) * mm});
            skLineSegment(sketch, "E123.top", {"start": v(-0.25, -125) * mm, "end": v(0.25, -125) * mm});
            skLineSegment(sketch, "E123.left", {"start": v(-0.25, 125) * mm, "end": v(-0.25, -125) * mm});
            skLineSegment(sketch, "E123.right", {"start": v(0.25, 125) * mm, "end": v(0.25, -125) * mm});
            skLineSegment(sketch, "E124", {"start": v(0, 125) * mm, "end": v(0, -125) * mm, "construction": true});
            skLineSegment(sketch, "E125", {"start": v(-0.25, 0) * mm, "end": v(0.25, 0) * mm, "construction": true});
            skSolve(sketch);
        }
        {
            var Q0;
            Q0 = qSketchRegion(id + "F5", true);
            extrude(context, id + "F6", {"entities" : qUnion([Q0]), "operationType" : NewBodyOperationType.REMOVE, "endBound" : BoundingType.THROUGH_ALL, "depth" : 25 * mm});
        }
        {
            var Q0;
            Q0=qCreatedBy(makeId("Right.planeOp"),FACE);
            var sketch = newSketch(context, id + "F7", { "sketchPlane" : qUnion([Q0])});
            skLineSegment(sketch, "E126", {"start": v(-82.87, 17.49) * mm, "end": v(82.87, 17.49) * mm, "construction": true});
            skLineSegment(sketch, "E127", {"start": v(0, 0) * mm, "end": v(0, 17.49) * mm});
            skCircle(sketch, "E128", {"center": v(-82.87, 17.49) * mm, "radius": 1.5 * mm});
            skCircle(sketch, "E129", {"center": v(82.87, 17.49) * mm, "radius": 1.5 * mm});
            skLineSegment(sketch, "E130", {"start": v(82.87, 0) * mm, "end": v(82.87, 22.74) * mm, "construction": true});
            skLineSegment(sketch, "E131", {"start": v(-82.87, 0) * mm, "end": v(-82.87, 32.17) * mm, "construction": true});
            skSolve(sketch);
        }
        {
            var Q0;
            Q0 = qSketchRegion(id + "F7", true);
            extrude(context, id + "F8", {"entities" : qUnion([Q0]), "operationType" : NewBodyOperationType.REMOVE, "endBound" : BoundingType.SYMMETRIC, "oppositeDirection" : true, "depth" : 3 * mm, "hasSecondDirection" : true, "secondDirectionOppositeDirection" : false, "secondDirectionDepth" : 3 * mm});
        }
    });
